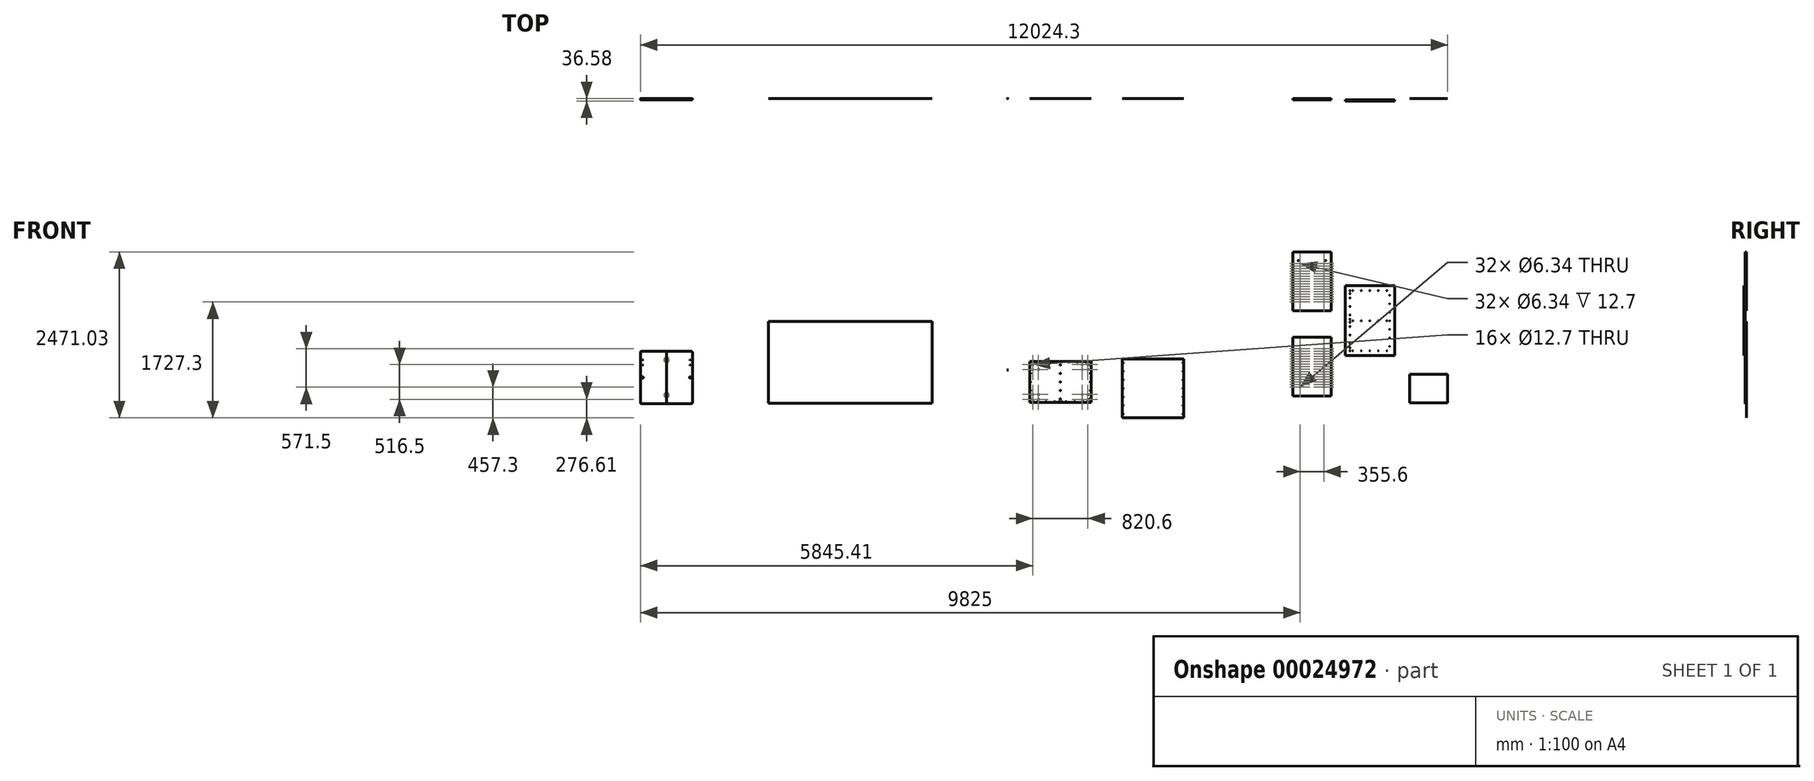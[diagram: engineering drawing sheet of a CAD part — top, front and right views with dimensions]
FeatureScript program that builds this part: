
annotation { "Feature Type Name" : "Feature", "Feature Type Description" : "" }
export const myFeature = defineFeature(function(context is Context, id is Id, definition is map)
    precondition{}
    {
        {
            var Q0;
            Q0=qCreatedBy(makeId("Front.planeOp"),FACE);
            var sketch = newSketch(context, id + "F0", { "sketchPlane" : qUnion([Q0])});
            skLineSegment(sketch, "E0.bottom", {"start": v(-504.26, 364.41) * mm, "end": v(54.54, 364.41) * mm});
            skLineSegment(sketch, "E0.top", {"start": v(-504.26, -245.19) * mm, "end": v(54.54, -245.19) * mm});
            skLineSegment(sketch, "E0.left", {"start": v(-529.66, 339.01) * mm, "end": v(-529.66, -219.79) * mm});
            skLineSegment(sketch, "E0.right", {"start": v(79.94, 339.01) * mm, "end": v(79.94, -219.79) * mm});
            skPoint(sketch, "E1.visualSharp", {"position": v(-529.66, 364.41) * mm});
            skArc(sketch, "E1.filletArc", {"start": v(-504.26, 364.41) * mm, "mid": v(-522.22, 356.97) * mm, "end": v(-529.66, 339.01) * mm});
            skPoint(sketch, "E2.visualSharp", {"position": v(79.94, 364.41) * mm});
            skArc(sketch, "E2.filletArc", {"start": v(79.94, 339.01) * mm, "mid": v(72.5, 356.97) * mm, "end": v(54.54, 364.41) * mm});
            skPoint(sketch, "E3.visualSharp", {"position": v(-529.66, -245.19) * mm});
            skArc(sketch, "E3.filletArc", {"start": v(-529.66, -219.79) * mm, "mid": v(-522.22, -237.75) * mm, "end": v(-504.26, -245.19) * mm});
            skPoint(sketch, "E4.visualSharp", {"position": v(79.94, -245.19) * mm});
            skArc(sketch, "E4.filletArc", {"start": v(54.54, -245.19) * mm, "mid": v(72.5, -237.75) * mm, "end": v(79.94, -219.79) * mm});
            skLineSegment(sketch, "E5.bottom", {"start": v(-529.66, 364.41) * mm, "end": v(-491.56, 364.41) * mm});
            skLineSegment(sketch, "E5.top", {"start": v(-529.66, 361.24) * mm, "end": v(-491.56, 361.24) * mm});
            skLineSegment(sketch, "E5.left", {"start": v(-529.66, 364.41) * mm, "end": v(-529.66, 361.24) * mm});
            skLineSegment(sketch, "E5.right", {"start": v(-491.56, 364.41) * mm, "end": v(-491.56, 361.24) * mm});
            skLineSegment(sketch, "E6.bottom", {"start": v(79.94, 364.41) * mm, "end": v(41.84, 364.41) * mm});
            skLineSegment(sketch, "E6.top", {"start": v(79.94, 361.24) * mm, "end": v(41.84, 361.24) * mm});
            skLineSegment(sketch, "E6.left", {"start": v(79.94, 364.41) * mm, "end": v(79.94, 361.24) * mm});
            skLineSegment(sketch, "E6.right", {"start": v(41.84, 364.41) * mm, "end": v(41.84, 361.24) * mm});
            skSolve(sketch);
        }
        {
            var Q0;
            {var subQ0=sQuery(id+"F0.wireOp",EDGE,"E5.left");Q0=makeQuery(id+"F0.imprint","IMPRINT",FACE,{"disambiguationData":[TD([[makeQuery(id+"F0.imprint","IMPRINT",EDGE,{"derivedFrom":subQ0}),1.0]])]});}
            var Q1;
            Q1=makeQuery(id+"F0.imprint","IMPRINT",FACE,{"disambiguationData":[TD([[makeQuery(id+"F0.imprint","IMPRINT",EDGE,{"derivedFrom":sQuery(id+"F0.wireOp",EDGE,"E0.bottom")}),-1.0]])]});
            var Q2;
            {var subQ0=sQuery(id+"F0.wireOp",EDGE,"E5.right");Q2=makeQuery(id+"F0.imprint","IMPRINT",FACE,{"disambiguationData":[TD([[makeQuery(id+"F0.imprint","IMPRINT",EDGE,{"derivedFrom":subQ0}),-1.0]])]});}
            extrude(context, id + "F1", {"entities" : qUnion([Q0, Q1, Q2]), "depth" : 23 / 812.8 * mm});
        }
        {
            var Q0;
            Q0=qCreatedBy(makeId("Front.planeOp"),FACE);
            var sketch = newSketch(context, id + "F2", { "sketchPlane" : qUnion([Q0])});
            skLineSegment(sketch, "E7.bottom", {"start": v(382.88, 489.15) * mm, "end": v(1297.28, 489.15) * mm});
            skLineSegment(sketch, "E7.top", {"start": v(382.88, -120.45) * mm, "end": v(1297.28, -120.45) * mm});
            skLineSegment(sketch, "E7.left", {"start": v(382.88, 489.15) * mm, "end": v(382.88, -120.45) * mm});
            skLineSegment(sketch, "E7.right", {"start": v(1297.28, 489.15) * mm, "end": v(1297.28, -120.45) * mm});
            skSolve(sketch);
        }
        {
            var Q0;
            Q0 = qSketchRegion(id + "F2", true);
            extrude(context, id + "F3", {"entities" : qUnion([Q0]), "depth" : 23 / 812.8 * mm});
        }
        {
            var Q0;
            Q0=qCreatedBy(makeId("Front.planeOp"),FACE);
            var sketch = newSketch(context, id + "F4", { "sketchPlane" : qUnion([Q0])});
            skLineSegment(sketch, "E8.bottom", {"start": v(1763.98, 527.36) * mm, "end": v(2678.38, 527.36) * mm});
            skLineSegment(sketch, "E8.top", {"start": v(1763.98, -350.51) * mm, "end": v(2678.38, -350.51) * mm});
            skLineSegment(sketch, "E8.left", {"start": v(1763.98, 527.36) * mm, "end": v(1763.98, -350.51) * mm});
            skLineSegment(sketch, "E8.right", {"start": v(2678.38, 527.36) * mm, "end": v(2678.38, -350.51) * mm});
            skSolve(sketch);
        }
        {
            var Q0;
            Q0=makeQuery(id+"F4.imprint","IMPRINT",FACE,{"disambiguationData":[TD([[makeQuery(id+"F4.imprint","IMPRINT",EDGE,{"derivedFrom":sQuery(id+"F4.wireOp",EDGE,"E8.bottom")}),-1.0]])]});
            extrude(context, id + "F5", {"entities" : qUnion([Q0]), "depth" : 23 / 812.8 * mm});
        }
        {
            var Q0;
            Q0=qCreatedBy(makeId("Front.planeOp"),FACE);
            var sketch = newSketch(context, id + "F6", { "sketchPlane" : qUnion([Q0])});
            skLineSegment(sketch, "E9.bottom", {"start": v(4301.03, 850.52) * mm, "end": v(4873.31, 850.52) * mm});
            skLineSegment(sketch, "E9.top", {"start": v(4301.03, -27.35) * mm, "end": v(4873.31, -27.35) * mm});
            skLineSegment(sketch, "E9.left", {"start": v(4301.03, 850.52) * mm, "end": v(4301.03, -27.35) * mm});
            skLineSegment(sketch, "E9.right", {"start": v(4873.31, 850.52) * mm, "end": v(4873.31, -27.35) * mm});
            skCircle(sketch, "E10", {"center": v(4383.97, 723.52) * mm, "radius": 3.97 * mm});
            skCircle(sketch, "E11", {"center": v(4790.37, 723.52) * mm, "radius": 3.97 * mm});
            skPoint(sketch, "E12", {"position": v(4587.17, 850.52) * mm});
            skCircle(sketch, "E13", {"center": v(4409.37, 106.79) * mm, "radius": 3.17 * mm});
            skCircle(sketch, "E14.0.1.0", {"center": v(4409.37, 144.89) * mm, "radius": 3.17 * mm});
            skCircle(sketch, "E14.0.2.0", {"center": v(4409.37, 182.99) * mm, "radius": 3.17 * mm});
            skCircle(sketch, "E14.0.3.0", {"center": v(4409.37, 221.09) * mm, "radius": 3.17 * mm});
            skCircle(sketch, "E14.0.4.0", {"center": v(4409.37, 259.19) * mm, "radius": 3.17 * mm});
            skCircle(sketch, "E14.0.5.0", {"center": v(4409.37, 297.29) * mm, "radius": 3.17 * mm});
            skCircle(sketch, "E14.0.6.0", {"center": v(4409.37, 335.39) * mm, "radius": 3.17 * mm});
            skCircle(sketch, "E14.0.7.0", {"center": v(4409.37, 373.49) * mm, "radius": 3.17 * mm});
            skCircle(sketch, "E14.0.8.0", {"center": v(4409.37, 411.59) * mm, "radius": 3.17 * mm});
            skCircle(sketch, "E14.0.9.0", {"center": v(4409.37, 449.69) * mm, "radius": 3.17 * mm});
            skCircle(sketch, "E14.0.10.0", {"center": v(4409.37, 487.79) * mm, "radius": 3.17 * mm});
            skCircle(sketch, "E14.0.11.0", {"center": v(4409.37, 525.89) * mm, "radius": 3.17 * mm});
            skCircle(sketch, "E14.0.12.0", {"center": v(4409.37, 563.99) * mm, "radius": 3.17 * mm});
            skCircle(sketch, "E14.0.13.0", {"center": v(4409.37, 602.09) * mm, "radius": 3.17 * mm});
            skCircle(sketch, "E14.0.14.0", {"center": v(4409.37, 640.19) * mm, "radius": 3.17 * mm});
            skCircle(sketch, "E14.0.15.0", {"center": v(4409.37, 678.29) * mm, "radius": 3.17 * mm});
            skCircle(sketch, "E14.1.0.0", {"center": v(4764.97, 106.79) * mm, "radius": 3.17 * mm});
            skCircle(sketch, "E14.1.1.0", {"center": v(4764.97, 144.89) * mm, "radius": 3.17 * mm});
            skCircle(sketch, "E14.1.2.0", {"center": v(4764.97, 182.99) * mm, "radius": 3.17 * mm});
            skCircle(sketch, "E14.1.3.0", {"center": v(4764.97, 221.09) * mm, "radius": 3.17 * mm});
            skCircle(sketch, "E14.1.4.0", {"center": v(4764.97, 259.19) * mm, "radius": 3.17 * mm});
            skCircle(sketch, "E14.1.5.0", {"center": v(4764.97, 297.29) * mm, "radius": 3.17 * mm});
            skCircle(sketch, "E14.1.6.0", {"center": v(4764.97, 335.39) * mm, "radius": 3.17 * mm});
            skCircle(sketch, "E14.1.7.0", {"center": v(4764.97, 373.49) * mm, "radius": 3.17 * mm});
            skCircle(sketch, "E14.1.8.0", {"center": v(4764.97, 411.59) * mm, "radius": 3.17 * mm});
            skCircle(sketch, "E14.1.9.0", {"center": v(4764.97, 449.69) * mm, "radius": 3.17 * mm});
            skCircle(sketch, "E14.1.10.0", {"center": v(4764.97, 487.79) * mm, "radius": 3.17 * mm});
            skCircle(sketch, "E14.1.11.0", {"center": v(4764.97, 525.89) * mm, "radius": 3.17 * mm});
            skCircle(sketch, "E14.1.12.0", {"center": v(4764.97, 563.99) * mm, "radius": 3.17 * mm});
            skCircle(sketch, "E14.1.13.0", {"center": v(4764.97, 602.09) * mm, "radius": 3.17 * mm});
            skCircle(sketch, "E14.1.14.0", {"center": v(4764.97, 640.19) * mm, "radius": 3.17 * mm});
            skCircle(sketch, "E14.1.15.0", {"center": v(4764.97, 678.29) * mm, "radius": 3.17 * mm});
            skLineSegment(sketch, "E14.direction1", {"start": v(4409.37, 106.79) * mm, "end": v(4764.97, 106.79) * mm, "construction": true});
            skLineSegment(sketch, "E14.direction2", {"start": v(4409.37, 106.79) * mm, "end": v(4409.37, 144.89) * mm, "construction": true});
            skSolve(sketch);
        }
        {
            var Q0;
            Q0=makeQuery(id+"F6.imprint","IMPRINT",FACE,{"disambiguationData":[TD([[makeQuery(id+"F6.imprint","IMPRINT",EDGE,{"derivedFrom":sQuery(id+"F6.wireOp",EDGE,"E9.bottom")}),-1.0]])]});
            extrude(context, id + "F7", {"entities" : qUnion([Q0]), "depth" : 23 / 812.8 * mm});
        }
        {
            var Q0;
            Q0=makeQuery(id+"F7.opExtrude","SWEPT_BODY",BODY,{"disambiguationData":[OSD([sQuery(id+"F6.wireOp",EDGE,"E9.bottom"),sQuery(id+"F6.wireOp",EDGE,"E9.top"),sQuery(id+"F6.wireOp",EDGE,"E9.left"),sQuery(id+"F6.wireOp",EDGE,"E9.right")])]});
            transform(context, id + "F8", {"entities" : qUnion([Q0]), "transformType" : TransformType.TRANSLATION_3D, "dx" : 914.4 * mm, "dy" : 0 * mm, "dz" : 0 * mm, "makeCopy" : true});
        }
        {
            var Q0;
            Q0=makeQuery(id+"F8.opPattern","COPY",BODY,{"derivedFrom":makeQuery(id+"F7.opExtrude","SWEPT_BODY",BODY,{"disambiguationData":[OSD([sQuery(id+"F6.wireOp",EDGE,"E9.bottom"),sQuery(id+"F6.wireOp",EDGE,"E9.top"),sQuery(id+"F6.wireOp",EDGE,"E9.left"),sQuery(id+"F6.wireOp",EDGE,"E9.right")])]}),"instanceName":"1"});
            transform(context, id + "F9", {"entities" : qUnion([Q0]), "transformType" : TransformType.TRANSLATION_3D, "dx" : 0 * mm, "dy" : 0 * mm, "dz" : 0 * mm, "makeCopy" : true});
        }
        {
            var Q0;
            Q0=makeQuery(id+"F9.opPattern","COPY",BODY,{"derivedFrom":makeQuery(id+"F8.opPattern","COPY",BODY,{"derivedFrom":makeQuery(id+"F7.opExtrude","SWEPT_BODY",BODY,{"disambiguationData":[OSD([sQuery(id+"F6.wireOp",EDGE,"E9.bottom"),sQuery(id+"F6.wireOp",EDGE,"E9.top"),sQuery(id+"F6.wireOp",EDGE,"E9.left"),sQuery(id+"F6.wireOp",EDGE,"E9.right")])]}),"instanceName":"1"}),"instanceName":"1"});
            deleteBodies(context, id + "F10", {"entities" : qUnion([Q0])});
        }
        {
            var Q0;
            Q0=makeQuery(id+"F8.opPattern","COPY",BODY,{"derivedFrom":makeQuery(id+"F7.opExtrude","SWEPT_BODY",BODY,{"disambiguationData":[OSD([sQuery(id+"F6.wireOp",EDGE,"E9.bottom"),sQuery(id+"F6.wireOp",EDGE,"E9.top"),sQuery(id+"F6.wireOp",EDGE,"E9.left"),sQuery(id+"F6.wireOp",EDGE,"E9.right")])]}),"instanceName":"1"});
            transform(context, id + "F11", {"entities" : qUnion([Q0]), "transformType" : TransformType.TRANSLATION_3D, "dx" : 914.4 * mm, "dy" : 0 * mm, "dz" : 0 * mm, "makeCopy" : true});
        }
        {
            var Q0;
            Q0=makeQuery(id+"F11.opPattern","COPY",FACE,{"derivedFrom":makeQuery(id+"F8.opPattern","COPY",FACE,{"derivedFrom":makeQuery(id+"F7.opExtrude","CAP_FACE",FACE,{"disambiguationData":[OSD([sQuery(id+"F6.wireOp",EDGE,"E9.bottom"),sQuery(id+"F6.wireOp",EDGE,"E9.top"),sQuery(id+"F6.wireOp",EDGE,"E9.left"),sQuery(id+"F6.wireOp",EDGE,"E9.right")])],"isStart":false}),"instanceName":"1"}),"instanceName":"1"});
            var sketch = newSketch(context, id + "F12", { "sketchPlane" : qUnion([Q0])});
            skLineSegment(sketch, "E15.bottom", {"start": v(6040.38, 295.61) * mm, "end": v(6608.7, 295.61) * mm});
            skLineSegment(sketch, "E15.top", {"start": v(6040.38, -129.84) * mm, "end": v(6608.7, -129.84) * mm});
            skLineSegment(sketch, "E15.left", {"start": v(6040.38, 295.61) * mm, "end": v(6040.38, -129.84) * mm});
            skLineSegment(sketch, "E15.right", {"start": v(6608.7, 295.61) * mm, "end": v(6608.7, -129.84) * mm});
            skSolve(sketch);
        }
        {
            var Q0;
            Q0 = qSketchRegion(id + "F12", true);
            extrude(context, id + "F13", {"entities" : qUnion([Q0]), "depth" : 23 / 812.8 * mm});
        }
        {
            var Q0;
            {var subQ0=sQuery(id+"F0.wireOp",EDGE,"E5.right");Q0=makeQuery(id+"F0.imprint","IMPRINT",FACE,{"disambiguationData":[TD([[makeQuery(id+"F0.imprint","IMPRINT",EDGE,{"derivedFrom":subQ0}),-1.0]])]});}
            extrude(context, id + "F14", {"entities" : qUnion([Q0]), "operationType" : NewBodyOperationType.REMOVE, "oppositeDirection" : true, "depth" : 25.4 * mm});
        }
        {
            var Q0;
            {var subQ0=sQuery(id+"F0.wireOp",EDGE,"E5.left");Q0=makeQuery(id+"F0.imprint","IMPRINT",FACE,{"disambiguationData":[TD([[makeQuery(id+"F0.imprint","IMPRINT",EDGE,{"derivedFrom":subQ0}),1.0]])]});}
            var Q1;
            {var subQ0=sQuery(id+"F0.wireOp",EDGE,"E5.right");Q1=makeQuery(id+"F0.imprint","IMPRINT",FACE,{"disambiguationData":[TD([[makeQuery(id+"F0.imprint","IMPRINT",EDGE,{"derivedFrom":subQ0}),-1.0]])]});}
            extrude(context, id + "F15", {"entities" : qUnion([Q0, Q1]), "depth" : 23 / 812.8 * mm});
        }
        {
            var Q0;
            Q0=makeQuery(id+"F15.opExtrude","SWEPT_BODY",BODY,{"disambiguationData":[OSD([sQuery(id+"F0.wireOp",EDGE,"E5.bottom"),sQuery(id+"F0.wireOp",EDGE,"E5.top"),sQuery(id+"F0.wireOp",EDGE,"E5.left"),sQuery(id+"F0.wireOp",EDGE,"E5.right")])]});
            var Q1;
            Q1=makeQuery(id+"F1.opExtrude","SWEPT_BODY",BODY,{"disambiguationData":[OSD([sQuery(id+"F0.wireOp",EDGE,"E0.bottom"),sQuery(id+"F0.wireOp",EDGE,"E0.top"),sQuery(id+"F0.wireOp",EDGE,"E0.left"),sQuery(id+"F0.wireOp",EDGE,"E0.right"),sQuery(id+"F0.wireOp",EDGE,"E1.filletArc"),sQuery(id+"F0.wireOp",EDGE,"E2.filletArc"),sQuery(id+"F0.wireOp",EDGE,"E3.filletArc"),sQuery(id+"F0.wireOp",EDGE,"E4.filletArc"),sQuery(id+"F0.wireOp",EDGE,"E5.bottom"),sQuery(id+"F0.wireOp",EDGE,"E5.top"),sQuery(id+"F0.wireOp",EDGE,"E5.left")])]});
            booleanBodies(context, id + "F16", {"operationType" : BooleanOperationType.SUBTRACTION, "tools" : qUnion([Q0]), "targets" : qUnion([Q1])});
        }
        {
            var Q0;
            Q0=makeQuery(id+"F5.opExtrude","SWEPT_BODY",BODY,{"disambiguationData":[OSD([sQuery(id+"F4.wireOp",EDGE,"E8.bottom"),sQuery(id+"F4.wireOp",EDGE,"E8.top"),sQuery(id+"F4.wireOp",EDGE,"E8.left"),sQuery(id+"F4.wireOp",EDGE,"E8.right")])]});
            transform(context, id + "F17", {"entities" : qUnion([Q0]), "transformType" : TransformType.TRANSLATION_3D, "dx" : 5080 * mm, "dy" : 0 * mm, "dz" : 0 * mm, "makeCopy" : true});
        }
        {
            var Q0;
            Q0=makeQuery(id+"F17.opPattern","COPY",BODY,{"derivedFrom":makeQuery(id+"F5.opExtrude","SWEPT_BODY",BODY,{"disambiguationData":[OSD([sQuery(id+"F4.wireOp",EDGE,"E8.bottom"),sQuery(id+"F4.wireOp",EDGE,"E8.top"),sQuery(id+"F4.wireOp",EDGE,"E8.left"),sQuery(id+"F4.wireOp",EDGE,"E8.right")])]}),"instanceName":"1"});
            deleteBodies(context, id + "F18", {"entities" : qUnion([Q0])});
        }
        {
            var Q0;
            Q0=makeQuery(id+"F13.opExtrude","CAP_FACE",FACE,{"disambiguationData":[OSD([sQuery(id+"F12.wireOp",EDGE,"E15.bottom"),sQuery(id+"F12.wireOp",EDGE,"E15.top"),sQuery(id+"F12.wireOp",EDGE,"E15.left"),sQuery(id+"F12.wireOp",EDGE,"E15.right")])],"isStart":false});
            var sketch = newSketch(context, id + "F19", { "sketchPlane" : qUnion([Q0])});
            skLineSegment(sketch, "E16.bottom", {"start": v(6912.5, 591.54) * mm, "end": v(7826.9, 591.54) * mm});
            skLineSegment(sketch, "E16.top", {"start": v(6912.5, -304.59) * mm, "end": v(7826.9, -304.59) * mm});
            skLineSegment(sketch, "E16.left", {"start": v(6912.5, 591.54) * mm, "end": v(6912.5, -304.59) * mm});
            skLineSegment(sketch, "E16.right", {"start": v(7826.9, 591.54) * mm, "end": v(7826.9, -304.59) * mm});
            skSolve(sketch);
        }
        {
            var Q0;
            Q0 = qSketchRegion(id + "F19", true);
            extrude(context, id + "F20", {"entities" : qUnion([Q0]), "depth" : 18.26 * mm});
        }
        {
            var Q0;
            Q0=makeQuery(id+"F20.opExtrude","CAP_FACE",FACE,{"disambiguationData":[OSD([sQuery(id+"F19.wireOp",EDGE,"E16.bottom"),sQuery(id+"F19.wireOp",EDGE,"E16.top"),sQuery(id+"F19.wireOp",EDGE,"E16.left"),sQuery(id+"F19.wireOp",EDGE,"E16.right")])],"isStart":false});
            var sketch = newSketch(context, id + "F21", { "sketchPlane" : qUnion([Q0])});
            skLineSegment(sketch, "E17.bottom", {"start": v(5080.39, 1616.94) * mm, "end": v(5816.99, 1616.94) * mm});
            skLineSegment(sketch, "E17.top", {"start": v(5080.39, 575.54) * mm, "end": v(5816.99, 575.54) * mm});
            skLineSegment(sketch, "E17.left", {"start": v(5080.39, 1616.94) * mm, "end": v(5080.39, 575.54) * mm});
            skLineSegment(sketch, "E17.right", {"start": v(5816.99, 1616.94) * mm, "end": v(5816.99, 575.54) * mm});
            skSolve(sketch);
        }
        {
            var Q0;
            Q0 = qSketchRegion(id + "F21", true);
            extrude(context, id + "F22", {"entities" : qUnion([Q0]), "depth" : 18.26 * mm});
        }
        {
            var Q0;
            Q0=makeQuery(id+"F1.opExtrude","CAP_FACE",FACE,{"disambiguationData":[OSD([sQuery(id+"F0.wireOp",EDGE,"E0.bottom"),sQuery(id+"F0.wireOp",EDGE,"E0.top"),sQuery(id+"F0.wireOp",EDGE,"E0.left"),sQuery(id+"F0.wireOp",EDGE,"E0.right"),sQuery(id+"F0.wireOp",EDGE,"E1.filletArc"),sQuery(id+"F0.wireOp",EDGE,"E2.filletArc"),sQuery(id+"F0.wireOp",EDGE,"E3.filletArc"),sQuery(id+"F0.wireOp",EDGE,"E4.filletArc"),sQuery(id+"F0.wireOp",EDGE,"E5.bottom"),sQuery(id+"F0.wireOp",EDGE,"E5.top"),sQuery(id+"F0.wireOp",EDGE,"E5.left"),sQuery(id+"F0.wireOp",EDGE,"E6.top"),sQuery(id+"F0.wireOp",EDGE,"E6.right")])],"isStart":true});
            fillet(context, id + "F23", {"entities" : qUnion([Q0]), "radius" : 12.7 * mm, "tangentPropagation" : true, "allowEdgeOverflow" : false});
        }
        {
            var Q0;
            Q0=makeQuery(id+"F7.opExtrude","SWEPT_BODY",BODY,{"disambiguationData":[OSD([sQuery(id+"F6.wireOp",EDGE,"E9.bottom"),sQuery(id+"F6.wireOp",EDGE,"E9.top"),sQuery(id+"F6.wireOp",EDGE,"E9.left"),sQuery(id+"F6.wireOp",EDGE,"E9.right")])]});
            deleteBodies(context, id + "F24", {"entities" : qUnion([Q0])});
        }
        {
            var Q0;
            Q0=makeQuery(id+"F20.opExtrude","SWEPT_BODY",BODY,{"disambiguationData":[OSD([sQuery(id+"F19.wireOp",EDGE,"E16.bottom"),sQuery(id+"F19.wireOp",EDGE,"E16.top"),sQuery(id+"F19.wireOp",EDGE,"E16.left"),sQuery(id+"F19.wireOp",EDGE,"E16.right")])]});
            deleteBodies(context, id + "F25", {"entities" : qUnion([Q0])});
        }
        {
            var Q0;
            Q0=qCreatedBy(makeId("Front.planeOp"),FACE);
            var sketch = newSketch(context, id + "F26", { "sketchPlane" : qUnion([Q0])});
            skLineSegment(sketch, "E18.bottom", {"start": v(-5028.28, 638.26) * mm, "end": v(-4653.63, 638.26) * mm});
            skLineSegment(sketch, "E18.top", {"start": v(-5028.28, -138.02) * mm, "end": v(-4653.63, -138.02) * mm});
            skLineSegment(sketch, "E18.left", {"start": v(-5028.28, 638.26) * mm, "end": v(-5028.28, -138.02) * mm});
            skLineSegment(sketch, "E18.right", {"start": v(-4640.93, 625.56) * mm, "end": v(-4640.93, -125.32) * mm});
            skPoint(sketch, "E19.visualSharp", {"position": v(-4640.93, -138.02) * mm});
            skArc(sketch, "E19.filletArc", {"start": v(-4653.63, -138.02) * mm, "mid": v(-4644.65, -134.3) * mm, "end": v(-4640.93, -125.32) * mm});
            skPoint(sketch, "E20.visualSharp", {"position": v(-4640.93, 638.26) * mm});
            skArc(sketch, "E20.filletArc", {"start": v(-4640.93, 625.56) * mm, "mid": v(-4644.65, 634.54) * mm, "end": v(-4653.63, 638.26) * mm});
            skCircle(sketch, "E21", {"center": v(-5007.64, 511.26) * mm, "radius": 17.5 * mm});
            skCircle(sketch, "E22", {"center": v(-5007.64, -11.02) * mm, "radius": 17.5 * mm});
            skCircle(sketch, "E23", {"center": v(-4999.64, 11.48) * mm, "radius": 4 * mm});
            skCircle(sketch, "E24", {"center": v(-4999.64, -33.52) * mm, "radius": 4 * mm});
            skCircle(sketch, "E25", {"center": v(-4999.64, 488.75) * mm, "radius": 4 * mm});
            skCircle(sketch, "E26", {"center": v(-4999.64, 533.76) * mm, "radius": 4 * mm});
            skCircle(sketch, "E27", {"center": v(-4675.85, 250.12) * mm, "radius": 9.52 * mm});
            skPoint(sketch, "E28", {"position": v(-4640.93, 250.12) * mm});
            skCircle(sketch, "E29", {"center": v(-4675.85, 435.06) * mm, "radius": 2.38 * mm});
            skCircle(sketch, "E30", {"center": v(-4675.85, 511.26) * mm, "radius": 2.38 * mm});
            skSolve(sketch);
        }
        {
            var Q0;
            Q0 = qSketchRegion(id + "F26", true);
            var Q1;
            Q1=makeQuery(id+"F26.imprint","IMPRINT",FACE,{"disambiguationData":[TD([[makeQuery(id+"F26.imprint","IMPRINT",EDGE,{"derivedFrom":sQuery(id+"F26.wireOp",EDGE,"E22")}),1.0]])]});
            var Q2;
            Q2=makeQuery(id+"F26.imprint","IMPRINT",FACE,{"disambiguationData":[TD([[makeQuery(id+"F26.imprint","IMPRINT",EDGE,{"derivedFrom":sQuery(id+"F26.wireOp",EDGE,"E23")}),1.0]])]});
            var Q3;
            Q3=makeQuery(id+"F26.imprint","IMPRINT",FACE,{"disambiguationData":[TD([[makeQuery(id+"F26.imprint","IMPRINT",EDGE,{"derivedFrom":sQuery(id+"F26.wireOp",EDGE,"E24")}),1.0]])]});
            var Q4;
            Q4=makeQuery(id+"F26.imprint","IMPRINT",FACE,{"disambiguationData":[TD([[makeQuery(id+"F26.imprint","IMPRINT",EDGE,{"derivedFrom":sQuery(id+"F26.wireOp",EDGE,"E21")}),1.0]])]});
            var Q5;
            Q5=makeQuery(id+"F26.imprint","IMPRINT",FACE,{"disambiguationData":[TD([[makeQuery(id+"F26.imprint","IMPRINT",EDGE,{"derivedFrom":sQuery(id+"F26.wireOp",EDGE,"E26")}),1.0]])]});
            var Q6;
            Q6=makeQuery(id+"F26.imprint","IMPRINT",FACE,{"disambiguationData":[TD([[makeQuery(id+"F26.imprint","IMPRINT",EDGE,{"derivedFrom":sQuery(id+"F26.wireOp",EDGE,"E25")}),1.0]])]});
            extrude(context, id + "F27", {"entities" : qUnion([Q0, Q1, Q2, Q3, Q4, Q5, Q6]), "depth" : 18.26 * mm});
        }
        {
            var Q0;
            Q0=makeQuery(id+"F27.opExtrude","CAP_EDGE",EDGE,{"disambiguationData":[OSD([sQuery(id+"F26.wireOp",EDGE,"E18.top")])],"isStart":true});
            var Q1;
            Q1=makeQuery(id+"F27.opExtrude","CAP_EDGE",EDGE,{"disambiguationData":[OSD([sQuery(id+"F26.wireOp",EDGE,"E18.right")])],"isStart":true});
            var Q2;
            Q2=makeQuery(id+"F27.opExtrude","CAP_EDGE",EDGE,{"disambiguationData":[OSD([sQuery(id+"F26.wireOp",EDGE,"E18.bottom")])],"isStart":true});
            fillet(context, id + "F28", {"entities" : qUnion([Q0, Q1, Q2]), "radius" : 6.35 * mm, "tangentPropagation" : true, "allowEdgeOverflow" : false});
        }
        {
            var Q0;
            Q0=makeQuery(id+"F27.opExtrude","CAP_EDGE",EDGE,{"disambiguationData":[OSD([sQuery(id+"F26.wireOp",EDGE,"E18.top")])],"isStart":false});
            var Q1;
            Q1=makeQuery(id+"F27.opExtrude","CAP_EDGE",EDGE,{"disambiguationData":[OSD([sQuery(id+"F26.wireOp",EDGE,"E18.right")])],"isStart":false});
            var Q2;
            Q2=makeQuery(id+"F27.opExtrude","CAP_EDGE",EDGE,{"disambiguationData":[OSD([sQuery(id+"F26.wireOp",EDGE,"E18.bottom")])],"isStart":false});
            fillet(context, id + "F29", {"entities" : qUnion([Q0, Q1, Q2]), "radius" : 6.35 * mm, "tangentPropagation" : true, "allowEdgeOverflow" : false});
        }
        {
            var Q0;
            Q0=makeQuery(id+"F26.imprint","IMPRINT",FACE,{"disambiguationData":[TD([[makeQuery(id+"F26.imprint","IMPRINT",EDGE,{"derivedFrom":sQuery(id+"F26.wireOp",EDGE,"E21")}),1.0]])]});
            extrude(context, id + "F30", {"entities" : qUnion([Q0]), "operationType" : NewBodyOperationType.REMOVE, "depth" : 12.7 * mm});
        }
        {
            var Q0;
            Q0=makeQuery(id+"F26.imprint","IMPRINT",FACE,{"disambiguationData":[TD([[makeQuery(id+"F26.imprint","IMPRINT",EDGE,{"derivedFrom":sQuery(id+"F26.wireOp",EDGE,"E25")}),1.0]])]});
            var Q1;
            Q1=makeQuery(id+"F26.imprint","IMPRINT",FACE,{"disambiguationData":[TD([[makeQuery(id+"F26.imprint","IMPRINT",EDGE,{"derivedFrom":sQuery(id+"F26.wireOp",EDGE,"E26")}),1.0]])]});
            extrude(context, id + "F31", {"entities" : qUnion([Q0, Q1]), "operationType" : NewBodyOperationType.REMOVE, "depth" : 12.7 * mm});
        }
        {
            var Q0;
            Q0=makeQuery(id+"F26.imprint","IMPRINT",FACE,{"disambiguationData":[TD([[makeQuery(id+"F26.imprint","IMPRINT",EDGE,{"derivedFrom":sQuery(id+"F26.wireOp",EDGE,"E22")}),1.0]])]});
            var Q1;
            Q1=makeQuery(id+"F26.imprint","IMPRINT",FACE,{"disambiguationData":[TD([[makeQuery(id+"F26.imprint","IMPRINT",EDGE,{"derivedFrom":sQuery(id+"F26.wireOp",EDGE,"E23")}),1.0]])]});
            var Q2;
            Q2=makeQuery(id+"F26.imprint","IMPRINT",FACE,{"disambiguationData":[TD([[makeQuery(id+"F26.imprint","IMPRINT",EDGE,{"derivedFrom":sQuery(id+"F26.wireOp",EDGE,"E24")}),1.0]])]});
            extrude(context, id + "F32", {"entities" : qUnion([Q0, Q1, Q2]), "operationType" : NewBodyOperationType.REMOVE, "depth" : 12.7 * mm});
        }
        {
            var Q0;
            Q0=makeQuery(id+"F11.opPattern","COPY",BODY,{"derivedFrom":makeQuery(id+"F8.opPattern","COPY",BODY,{"derivedFrom":makeQuery(id+"F7.opExtrude","SWEPT_BODY",BODY,{"disambiguationData":[OSD([sQuery(id+"F6.wireOp",EDGE,"E9.bottom"),sQuery(id+"F6.wireOp",EDGE,"E9.top"),sQuery(id+"F6.wireOp",EDGE,"E9.left"),sQuery(id+"F6.wireOp",EDGE,"E9.right"),sQuery(id+"F6.wireOp",EDGE,"E10"),sQuery(id+"F6.wireOp",EDGE,"E11")])]}),"instanceName":"1"}),"instanceName":"1"});
            deleteBodies(context, id + "F33", {"entities" : qUnion([Q0])});
        }
        {
            var Q0;
            Q0=makeQuery(id+"F6.imprint","IMPRINT",FACE,{"disambiguationData":[TD([[makeQuery(id+"F6.imprint","IMPRINT",EDGE,{"derivedFrom":sQuery(id+"F6.wireOp",EDGE,"E14.1.8.0")}),1.0]])]});
            var Q1;
            Q1=makeQuery(id+"F6.imprint","IMPRINT",FACE,{"disambiguationData":[TD([[makeQuery(id+"F6.imprint","IMPRINT",EDGE,{"derivedFrom":sQuery(id+"F6.wireOp",EDGE,"E14.1.7.0")}),1.0]])]});
            var Q2;
            Q2=makeQuery(id+"F6.imprint","IMPRINT",FACE,{"disambiguationData":[TD([[makeQuery(id+"F6.imprint","IMPRINT",EDGE,{"derivedFrom":sQuery(id+"F6.wireOp",EDGE,"E14.1.6.0")}),1.0]])]});
            var Q3;
            Q3=makeQuery(id+"F6.imprint","IMPRINT",FACE,{"disambiguationData":[TD([[makeQuery(id+"F6.imprint","IMPRINT",EDGE,{"derivedFrom":sQuery(id+"F6.wireOp",EDGE,"E14.1.4.0")}),1.0]])]});
            var Q4;
            Q4=makeQuery(id+"F6.imprint","IMPRINT",FACE,{"disambiguationData":[TD([[makeQuery(id+"F6.imprint","IMPRINT",EDGE,{"derivedFrom":sQuery(id+"F6.wireOp",EDGE,"E14.1.10.0")}),1.0]])]});
            var Q5;
            Q5=makeQuery(id+"F6.imprint","IMPRINT",FACE,{"disambiguationData":[TD([[makeQuery(id+"F6.imprint","IMPRINT",EDGE,{"derivedFrom":sQuery(id+"F6.wireOp",EDGE,"E14.1.2.0")}),1.0]])]});
            var Q6;
            Q6=makeQuery(id+"F6.imprint","IMPRINT",FACE,{"disambiguationData":[TD([[makeQuery(id+"F6.imprint","IMPRINT",EDGE,{"derivedFrom":sQuery(id+"F6.wireOp",EDGE,"E14.1.1.0")}),1.0]])]});
            var Q7;
            Q7=makeQuery(id+"F6.imprint","IMPRINT",FACE,{"disambiguationData":[TD([[makeQuery(id+"F6.imprint","IMPRINT",EDGE,{"derivedFrom":sQuery(id+"F6.wireOp",EDGE,"E14.1.14.0")}),1.0]])]});
            var Q8;
            Q8=makeQuery(id+"F6.imprint","IMPRINT",FACE,{"disambiguationData":[TD([[makeQuery(id+"F6.imprint","IMPRINT",EDGE,{"derivedFrom":sQuery(id+"F6.wireOp",EDGE,"E14.1.3.0")}),1.0]])]});
            var Q9;
            Q9=makeQuery(id+"F6.imprint","IMPRINT",FACE,{"disambiguationData":[TD([[makeQuery(id+"F6.imprint","IMPRINT",EDGE,{"derivedFrom":sQuery(id+"F6.wireOp",EDGE,"E14.1.11.0")}),1.0]])]});
            var Q10;
            Q10=makeQuery(id+"F6.imprint","IMPRINT",FACE,{"disambiguationData":[TD([[makeQuery(id+"F6.imprint","IMPRINT",EDGE,{"derivedFrom":sQuery(id+"F6.wireOp",EDGE,"E14.1.12.0")}),1.0]])]});
            var Q11;
            Q11=makeQuery(id+"F6.imprint","IMPRINT",FACE,{"disambiguationData":[TD([[makeQuery(id+"F6.imprint","IMPRINT",EDGE,{"derivedFrom":sQuery(id+"F6.wireOp",EDGE,"E14.1.15.0")}),1.0]])]});
            var Q12;
            Q12=makeQuery(id+"F6.imprint","IMPRINT",FACE,{"disambiguationData":[TD([[makeQuery(id+"F6.imprint","IMPRINT",EDGE,{"derivedFrom":sQuery(id+"F6.wireOp",EDGE,"E14.1.9.0")}),1.0]])]});
            var Q13;
            Q13=makeQuery(id+"F6.imprint","IMPRINT",FACE,{"disambiguationData":[TD([[makeQuery(id+"F6.imprint","IMPRINT",EDGE,{"derivedFrom":sQuery(id+"F6.wireOp",EDGE,"E14.1.5.0")}),1.0]])]});
            var Q14;
            Q14=makeQuery(id+"F6.imprint","IMPRINT",FACE,{"disambiguationData":[TD([[makeQuery(id+"F6.imprint","IMPRINT",EDGE,{"derivedFrom":sQuery(id+"F6.wireOp",EDGE,"E14.1.13.0")}),1.0]])]});
            var Q15;
            Q15=makeQuery(id+"F6.imprint","IMPRINT",FACE,{"disambiguationData":[TD([[makeQuery(id+"F6.imprint","IMPRINT",EDGE,{"derivedFrom":sQuery(id+"F6.wireOp",EDGE,"E14.1.0.0")}),1.0]])]});
            var Q16;
            Q16=makeQuery(id+"F6.imprint","IMPRINT",FACE,{"disambiguationData":[TD([[makeQuery(id+"F6.imprint","IMPRINT",EDGE,{"derivedFrom":sQuery(id+"F6.wireOp",EDGE,"E14.0.11.0")}),1.0]])]});
            var Q17;
            Q17=makeQuery(id+"F6.imprint","IMPRINT",FACE,{"disambiguationData":[TD([[makeQuery(id+"F6.imprint","IMPRINT",EDGE,{"derivedFrom":sQuery(id+"F6.wireOp",EDGE,"E14.0.15.0")}),1.0]])]});
            var Q18;
            Q18=makeQuery(id+"F6.imprint","IMPRINT",FACE,{"disambiguationData":[TD([[makeQuery(id+"F6.imprint","IMPRINT",EDGE,{"derivedFrom":sQuery(id+"F6.wireOp",EDGE,"E14.0.14.0")}),1.0]])]});
            var Q19;
            Q19=makeQuery(id+"F6.imprint","IMPRINT",FACE,{"disambiguationData":[TD([[makeQuery(id+"F6.imprint","IMPRINT",EDGE,{"derivedFrom":sQuery(id+"F6.wireOp",EDGE,"E14.0.13.0")}),1.0]])]});
            var Q20;
            Q20=makeQuery(id+"F6.imprint","IMPRINT",FACE,{"disambiguationData":[TD([[makeQuery(id+"F6.imprint","IMPRINT",EDGE,{"derivedFrom":sQuery(id+"F6.wireOp",EDGE,"E14.0.12.0")}),1.0]])]});
            var Q21;
            Q21=makeQuery(id+"F6.imprint","IMPRINT",FACE,{"disambiguationData":[TD([[makeQuery(id+"F6.imprint","IMPRINT",EDGE,{"derivedFrom":sQuery(id+"F6.wireOp",EDGE,"E14.0.3.0")}),1.0]])]});
            var Q22;
            Q22=makeQuery(id+"F6.imprint","IMPRINT",FACE,{"disambiguationData":[TD([[makeQuery(id+"F6.imprint","IMPRINT",EDGE,{"derivedFrom":sQuery(id+"F6.wireOp",EDGE,"E14.0.2.0")}),1.0]])]});
            var Q23;
            Q23=makeQuery(id+"F6.imprint","IMPRINT",FACE,{"disambiguationData":[TD([[makeQuery(id+"F6.imprint","IMPRINT",EDGE,{"derivedFrom":sQuery(id+"F6.wireOp",EDGE,"E14.0.4.0")}),1.0]])]});
            var Q24;
            Q24=makeQuery(id+"F6.imprint","IMPRINT",FACE,{"disambiguationData":[TD([[makeQuery(id+"F6.imprint","IMPRINT",EDGE,{"derivedFrom":sQuery(id+"F6.wireOp",EDGE,"E14.0.5.0")}),1.0]])]});
            var Q25;
            Q25=makeQuery(id+"F6.imprint","IMPRINT",FACE,{"disambiguationData":[TD([[makeQuery(id+"F6.imprint","IMPRINT",EDGE,{"derivedFrom":sQuery(id+"F6.wireOp",EDGE,"E14.0.6.0")}),1.0]])]});
            var Q26;
            Q26=makeQuery(id+"F6.imprint","IMPRINT",FACE,{"disambiguationData":[TD([[makeQuery(id+"F6.imprint","IMPRINT",EDGE,{"derivedFrom":sQuery(id+"F6.wireOp",EDGE,"E14.0.7.0")}),1.0]])]});
            var Q27;
            Q27=makeQuery(id+"F6.imprint","IMPRINT",FACE,{"disambiguationData":[TD([[makeQuery(id+"F6.imprint","IMPRINT",EDGE,{"derivedFrom":sQuery(id+"F6.wireOp",EDGE,"E14.0.8.0")}),1.0]])]});
            var Q28;
            Q28=makeQuery(id+"F6.imprint","IMPRINT",FACE,{"disambiguationData":[TD([[makeQuery(id+"F6.imprint","IMPRINT",EDGE,{"derivedFrom":sQuery(id+"F6.wireOp",EDGE,"E14.0.9.0")}),1.0]])]});
            var Q29;
            Q29=makeQuery(id+"F6.imprint","IMPRINT",FACE,{"disambiguationData":[TD([[makeQuery(id+"F6.imprint","IMPRINT",EDGE,{"derivedFrom":sQuery(id+"F6.wireOp",EDGE,"E14.0.10.0")}),1.0]])]});
            var Q30;
            Q30=makeQuery(id+"F6.imprint","IMPRINT",FACE,{"disambiguationData":[TD([[makeQuery(id+"F6.imprint","IMPRINT",EDGE,{"derivedFrom":sQuery(id+"F6.wireOp",EDGE,"E14.0.1.0")}),1.0]])]});
            var Q31;
            Q31=makeQuery(id+"F6.imprint","IMPRINT",FACE,{"disambiguationData":[TD([[makeQuery(id+"F6.imprint","IMPRINT",EDGE,{"derivedFrom":sQuery(id+"F6.wireOp",EDGE,"E13")}),1.0]])]});
            var Q32;
            Q32=makeQuery(id+"F6.imprint","IMPRINT",FACE,{"disambiguationData":[TD([[makeQuery(id+"F6.imprint","IMPRINT",EDGE,{"derivedFrom":sQuery(id+"F6.wireOp",EDGE,"E9.bottom")}),-1.0]])]});
            extrude(context, id + "F34", {"entities" : qUnion([Q0, Q1, Q2, Q3, Q4, Q5, Q6, Q7, Q8, Q9, Q10, Q11, Q12, Q13, Q14, Q15, Q16, Q17, Q18, Q19, Q20, Q21, Q22, Q23, Q24, Q25, Q26, Q27, Q28, Q29, Q30, Q31, Q32]), "depth" : 18.26 * mm});
        }
        {
            var Q0;
            Q0=makeQuery(id+"F34.opExtrude","SWEPT_BODY",BODY,{"disambiguationData":[OSD([sQuery(id+"F6.wireOp",EDGE,"E9.bottom"),sQuery(id+"F6.wireOp",EDGE,"E9.top"),sQuery(id+"F6.wireOp",EDGE,"E9.left"),sQuery(id+"F6.wireOp",EDGE,"E9.right"),sQuery(id+"F6.wireOp",EDGE,"E10"),sQuery(id+"F6.wireOp",EDGE,"E11")])]});
            transform(context, id + "F35", {"entities" : qUnion([Q0]), "transformType" : TransformType.TRANSLATION_3D, "dx" : 0 * mm, "dy" : 0 * mm, "dz" : 1270 * mm, "makeCopy" : false});
        }
        {
            var Q0;
            Q0=makeQuery(id+"F6.imprint","IMPRINT",FACE,{"disambiguationData":[TD([[makeQuery(id+"F6.imprint","IMPRINT",EDGE,{"derivedFrom":sQuery(id+"F6.wireOp",EDGE,"E9.bottom")}),-1.0]])]});
            var Q1;
            Q1=makeQuery(id+"F6.imprint","IMPRINT",FACE,{"disambiguationData":[TD([[makeQuery(id+"F6.imprint","IMPRINT",EDGE,{"derivedFrom":sQuery(id+"F6.wireOp",EDGE,"E14.0.11.0")}),1.0]])]});
            var Q2;
            Q2=makeQuery(id+"F6.imprint","IMPRINT",FACE,{"disambiguationData":[TD([[makeQuery(id+"F6.imprint","IMPRINT",EDGE,{"derivedFrom":sQuery(id+"F6.wireOp",EDGE,"E14.0.15.0")}),1.0]])]});
            var Q3;
            Q3=makeQuery(id+"F6.imprint","IMPRINT",FACE,{"disambiguationData":[TD([[makeQuery(id+"F6.imprint","IMPRINT",EDGE,{"derivedFrom":sQuery(id+"F6.wireOp",EDGE,"E14.0.14.0")}),1.0]])]});
            var Q4;
            Q4=makeQuery(id+"F6.imprint","IMPRINT",FACE,{"disambiguationData":[TD([[makeQuery(id+"F6.imprint","IMPRINT",EDGE,{"derivedFrom":sQuery(id+"F6.wireOp",EDGE,"E14.0.13.0")}),1.0]])]});
            var Q5;
            Q5=makeQuery(id+"F6.imprint","IMPRINT",FACE,{"disambiguationData":[TD([[makeQuery(id+"F6.imprint","IMPRINT",EDGE,{"derivedFrom":sQuery(id+"F6.wireOp",EDGE,"E14.0.12.0")}),1.0]])]});
            var Q6;
            Q6=makeQuery(id+"F6.imprint","IMPRINT",FACE,{"disambiguationData":[TD([[makeQuery(id+"F6.imprint","IMPRINT",EDGE,{"derivedFrom":sQuery(id+"F6.wireOp",EDGE,"E14.0.3.0")}),1.0]])]});
            var Q7;
            Q7=makeQuery(id+"F6.imprint","IMPRINT",FACE,{"disambiguationData":[TD([[makeQuery(id+"F6.imprint","IMPRINT",EDGE,{"derivedFrom":sQuery(id+"F6.wireOp",EDGE,"E14.0.2.0")}),1.0]])]});
            var Q8;
            Q8=makeQuery(id+"F6.imprint","IMPRINT",FACE,{"disambiguationData":[TD([[makeQuery(id+"F6.imprint","IMPRINT",EDGE,{"derivedFrom":sQuery(id+"F6.wireOp",EDGE,"E14.0.4.0")}),1.0]])]});
            var Q9;
            Q9=makeQuery(id+"F6.imprint","IMPRINT",FACE,{"disambiguationData":[TD([[makeQuery(id+"F6.imprint","IMPRINT",EDGE,{"derivedFrom":sQuery(id+"F6.wireOp",EDGE,"E14.0.5.0")}),1.0]])]});
            var Q10;
            Q10=makeQuery(id+"F6.imprint","IMPRINT",FACE,{"disambiguationData":[TD([[makeQuery(id+"F6.imprint","IMPRINT",EDGE,{"derivedFrom":sQuery(id+"F6.wireOp",EDGE,"E14.0.6.0")}),1.0]])]});
            var Q11;
            Q11=makeQuery(id+"F6.imprint","IMPRINT",FACE,{"disambiguationData":[TD([[makeQuery(id+"F6.imprint","IMPRINT",EDGE,{"derivedFrom":sQuery(id+"F6.wireOp",EDGE,"E14.0.7.0")}),1.0]])]});
            var Q12;
            Q12=makeQuery(id+"F6.imprint","IMPRINT",FACE,{"disambiguationData":[TD([[makeQuery(id+"F6.imprint","IMPRINT",EDGE,{"derivedFrom":sQuery(id+"F6.wireOp",EDGE,"E14.0.8.0")}),1.0]])]});
            var Q13;
            Q13=makeQuery(id+"F6.imprint","IMPRINT",FACE,{"disambiguationData":[TD([[makeQuery(id+"F6.imprint","IMPRINT",EDGE,{"derivedFrom":sQuery(id+"F6.wireOp",EDGE,"E14.0.9.0")}),1.0]])]});
            var Q14;
            Q14=makeQuery(id+"F6.imprint","IMPRINT",FACE,{"disambiguationData":[TD([[makeQuery(id+"F6.imprint","IMPRINT",EDGE,{"derivedFrom":sQuery(id+"F6.wireOp",EDGE,"E14.0.10.0")}),1.0]])]});
            var Q15;
            Q15=makeQuery(id+"F6.imprint","IMPRINT",FACE,{"disambiguationData":[TD([[makeQuery(id+"F6.imprint","IMPRINT",EDGE,{"derivedFrom":sQuery(id+"F6.wireOp",EDGE,"E14.0.1.0")}),1.0]])]});
            var Q16;
            Q16=makeQuery(id+"F6.imprint","IMPRINT",FACE,{"disambiguationData":[TD([[makeQuery(id+"F6.imprint","IMPRINT",EDGE,{"derivedFrom":sQuery(id+"F6.wireOp",EDGE,"E13")}),1.0]])]});
            var Q17;
            Q17=makeQuery(id+"F6.imprint","IMPRINT",FACE,{"disambiguationData":[TD([[makeQuery(id+"F6.imprint","IMPRINT",EDGE,{"derivedFrom":sQuery(id+"F6.wireOp",EDGE,"E14.1.8.0")}),1.0]])]});
            var Q18;
            Q18=makeQuery(id+"F6.imprint","IMPRINT",FACE,{"disambiguationData":[TD([[makeQuery(id+"F6.imprint","IMPRINT",EDGE,{"derivedFrom":sQuery(id+"F6.wireOp",EDGE,"E14.1.7.0")}),1.0]])]});
            var Q19;
            Q19=makeQuery(id+"F6.imprint","IMPRINT",FACE,{"disambiguationData":[TD([[makeQuery(id+"F6.imprint","IMPRINT",EDGE,{"derivedFrom":sQuery(id+"F6.wireOp",EDGE,"E14.1.6.0")}),1.0]])]});
            var Q20;
            Q20=makeQuery(id+"F6.imprint","IMPRINT",FACE,{"disambiguationData":[TD([[makeQuery(id+"F6.imprint","IMPRINT",EDGE,{"derivedFrom":sQuery(id+"F6.wireOp",EDGE,"E14.1.4.0")}),1.0]])]});
            var Q21;
            Q21=makeQuery(id+"F6.imprint","IMPRINT",FACE,{"disambiguationData":[TD([[makeQuery(id+"F6.imprint","IMPRINT",EDGE,{"derivedFrom":sQuery(id+"F6.wireOp",EDGE,"E14.1.10.0")}),1.0]])]});
            var Q22;
            Q22=makeQuery(id+"F6.imprint","IMPRINT",FACE,{"disambiguationData":[TD([[makeQuery(id+"F6.imprint","IMPRINT",EDGE,{"derivedFrom":sQuery(id+"F6.wireOp",EDGE,"E14.1.2.0")}),1.0]])]});
            var Q23;
            Q23=makeQuery(id+"F6.imprint","IMPRINT",FACE,{"disambiguationData":[TD([[makeQuery(id+"F6.imprint","IMPRINT",EDGE,{"derivedFrom":sQuery(id+"F6.wireOp",EDGE,"E14.1.1.0")}),1.0]])]});
            var Q24;
            Q24=makeQuery(id+"F6.imprint","IMPRINT",FACE,{"disambiguationData":[TD([[makeQuery(id+"F6.imprint","IMPRINT",EDGE,{"derivedFrom":sQuery(id+"F6.wireOp",EDGE,"E14.1.14.0")}),1.0]])]});
            var Q25;
            Q25=makeQuery(id+"F6.imprint","IMPRINT",FACE,{"disambiguationData":[TD([[makeQuery(id+"F6.imprint","IMPRINT",EDGE,{"derivedFrom":sQuery(id+"F6.wireOp",EDGE,"E14.1.3.0")}),1.0]])]});
            var Q26;
            Q26=makeQuery(id+"F6.imprint","IMPRINT",FACE,{"disambiguationData":[TD([[makeQuery(id+"F6.imprint","IMPRINT",EDGE,{"derivedFrom":sQuery(id+"F6.wireOp",EDGE,"E14.1.11.0")}),1.0]])]});
            var Q27;
            Q27=makeQuery(id+"F6.imprint","IMPRINT",FACE,{"disambiguationData":[TD([[makeQuery(id+"F6.imprint","IMPRINT",EDGE,{"derivedFrom":sQuery(id+"F6.wireOp",EDGE,"E14.1.12.0")}),1.0]])]});
            var Q28;
            Q28=makeQuery(id+"F6.imprint","IMPRINT",FACE,{"disambiguationData":[TD([[makeQuery(id+"F6.imprint","IMPRINT",EDGE,{"derivedFrom":sQuery(id+"F6.wireOp",EDGE,"E14.1.15.0")}),1.0]])]});
            var Q29;
            Q29=makeQuery(id+"F6.imprint","IMPRINT",FACE,{"disambiguationData":[TD([[makeQuery(id+"F6.imprint","IMPRINT",EDGE,{"derivedFrom":sQuery(id+"F6.wireOp",EDGE,"E14.1.9.0")}),1.0]])]});
            var Q30;
            Q30=makeQuery(id+"F6.imprint","IMPRINT",FACE,{"disambiguationData":[TD([[makeQuery(id+"F6.imprint","IMPRINT",EDGE,{"derivedFrom":sQuery(id+"F6.wireOp",EDGE,"E14.1.5.0")}),1.0]])]});
            var Q31;
            Q31=makeQuery(id+"F6.imprint","IMPRINT",FACE,{"disambiguationData":[TD([[makeQuery(id+"F6.imprint","IMPRINT",EDGE,{"derivedFrom":sQuery(id+"F6.wireOp",EDGE,"E14.1.13.0")}),1.0]])]});
            var Q32;
            Q32=makeQuery(id+"F6.imprint","IMPRINT",FACE,{"disambiguationData":[TD([[makeQuery(id+"F6.imprint","IMPRINT",EDGE,{"derivedFrom":sQuery(id+"F6.wireOp",EDGE,"E14.1.0.0")}),1.0]])]});
            extrude(context, id + "F36", {"entities" : qUnion([Q0, Q1, Q2, Q3, Q4, Q5, Q6, Q7, Q8, Q9, Q10, Q11, Q12, Q13, Q14, Q15, Q16, Q17, Q18, Q19, Q20, Q21, Q22, Q23, Q24, Q25, Q26, Q27, Q28, Q29, Q30, Q31, Q32]), "depth" : 18.26 * mm});
        }
        {
            var Q0;
            Q0=makeQuery(id+"F6.imprint","IMPRINT",FACE,{"disambiguationData":[TD([[makeQuery(id+"F6.imprint","IMPRINT",EDGE,{"derivedFrom":sQuery(id+"F6.wireOp",EDGE,"E9.bottom")}),-1.0]])]});
            var Q1;
            Q1=makeQuery(id+"F6.imprint","IMPRINT",FACE,{"disambiguationData":[TD([[makeQuery(id+"F6.imprint","IMPRINT",EDGE,{"derivedFrom":sQuery(id+"F6.wireOp",EDGE,"E14.0.11.0")}),1.0]])]});
            var Q2;
            Q2=makeQuery(id+"F6.imprint","IMPRINT",FACE,{"disambiguationData":[TD([[makeQuery(id+"F6.imprint","IMPRINT",EDGE,{"derivedFrom":sQuery(id+"F6.wireOp",EDGE,"E14.0.15.0")}),1.0]])]});
            var Q3;
            Q3=makeQuery(id+"F6.imprint","IMPRINT",FACE,{"disambiguationData":[TD([[makeQuery(id+"F6.imprint","IMPRINT",EDGE,{"derivedFrom":sQuery(id+"F6.wireOp",EDGE,"E14.0.14.0")}),1.0]])]});
            var Q4;
            Q4=makeQuery(id+"F6.imprint","IMPRINT",FACE,{"disambiguationData":[TD([[makeQuery(id+"F6.imprint","IMPRINT",EDGE,{"derivedFrom":sQuery(id+"F6.wireOp",EDGE,"E14.0.13.0")}),1.0]])]});
            var Q5;
            Q5=makeQuery(id+"F6.imprint","IMPRINT",FACE,{"disambiguationData":[TD([[makeQuery(id+"F6.imprint","IMPRINT",EDGE,{"derivedFrom":sQuery(id+"F6.wireOp",EDGE,"E14.0.12.0")}),1.0]])]});
            var Q6;
            Q6=makeQuery(id+"F6.imprint","IMPRINT",FACE,{"disambiguationData":[TD([[makeQuery(id+"F6.imprint","IMPRINT",EDGE,{"derivedFrom":sQuery(id+"F6.wireOp",EDGE,"E14.0.3.0")}),1.0]])]});
            var Q7;
            Q7=makeQuery(id+"F6.imprint","IMPRINT",FACE,{"disambiguationData":[TD([[makeQuery(id+"F6.imprint","IMPRINT",EDGE,{"derivedFrom":sQuery(id+"F6.wireOp",EDGE,"E14.0.2.0")}),1.0]])]});
            var Q8;
            Q8=makeQuery(id+"F6.imprint","IMPRINT",FACE,{"disambiguationData":[TD([[makeQuery(id+"F6.imprint","IMPRINT",EDGE,{"derivedFrom":sQuery(id+"F6.wireOp",EDGE,"E14.0.4.0")}),1.0]])]});
            var Q9;
            Q9=makeQuery(id+"F6.imprint","IMPRINT",FACE,{"disambiguationData":[TD([[makeQuery(id+"F6.imprint","IMPRINT",EDGE,{"derivedFrom":sQuery(id+"F6.wireOp",EDGE,"E14.0.5.0")}),1.0]])]});
            var Q10;
            Q10=makeQuery(id+"F6.imprint","IMPRINT",FACE,{"disambiguationData":[TD([[makeQuery(id+"F6.imprint","IMPRINT",EDGE,{"derivedFrom":sQuery(id+"F6.wireOp",EDGE,"E14.0.6.0")}),1.0]])]});
            var Q11;
            Q11=makeQuery(id+"F6.imprint","IMPRINT",FACE,{"disambiguationData":[TD([[makeQuery(id+"F6.imprint","IMPRINT",EDGE,{"derivedFrom":sQuery(id+"F6.wireOp",EDGE,"E14.0.7.0")}),1.0]])]});
            var Q12;
            Q12=makeQuery(id+"F6.imprint","IMPRINT",FACE,{"disambiguationData":[TD([[makeQuery(id+"F6.imprint","IMPRINT",EDGE,{"derivedFrom":sQuery(id+"F6.wireOp",EDGE,"E14.0.8.0")}),1.0]])]});
            var Q13;
            Q13=makeQuery(id+"F6.imprint","IMPRINT",FACE,{"disambiguationData":[TD([[makeQuery(id+"F6.imprint","IMPRINT",EDGE,{"derivedFrom":sQuery(id+"F6.wireOp",EDGE,"E14.0.9.0")}),1.0]])]});
            var Q14;
            Q14=makeQuery(id+"F6.imprint","IMPRINT",FACE,{"disambiguationData":[TD([[makeQuery(id+"F6.imprint","IMPRINT",EDGE,{"derivedFrom":sQuery(id+"F6.wireOp",EDGE,"E14.0.10.0")}),1.0]])]});
            var Q15;
            Q15=makeQuery(id+"F6.imprint","IMPRINT",FACE,{"disambiguationData":[TD([[makeQuery(id+"F6.imprint","IMPRINT",EDGE,{"derivedFrom":sQuery(id+"F6.wireOp",EDGE,"E14.0.1.0")}),1.0]])]});
            var Q16;
            Q16=makeQuery(id+"F6.imprint","IMPRINT",FACE,{"disambiguationData":[TD([[makeQuery(id+"F6.imprint","IMPRINT",EDGE,{"derivedFrom":sQuery(id+"F6.wireOp",EDGE,"E13")}),1.0]])]});
            var Q17;
            Q17=makeQuery(id+"F6.imprint","IMPRINT",FACE,{"disambiguationData":[TD([[makeQuery(id+"F6.imprint","IMPRINT",EDGE,{"derivedFrom":sQuery(id+"F6.wireOp",EDGE,"E14.1.8.0")}),1.0]])]});
            var Q18;
            Q18=makeQuery(id+"F6.imprint","IMPRINT",FACE,{"disambiguationData":[TD([[makeQuery(id+"F6.imprint","IMPRINT",EDGE,{"derivedFrom":sQuery(id+"F6.wireOp",EDGE,"E14.1.7.0")}),1.0]])]});
            var Q19;
            Q19=makeQuery(id+"F6.imprint","IMPRINT",FACE,{"disambiguationData":[TD([[makeQuery(id+"F6.imprint","IMPRINT",EDGE,{"derivedFrom":sQuery(id+"F6.wireOp",EDGE,"E14.1.6.0")}),1.0]])]});
            var Q20;
            Q20=makeQuery(id+"F6.imprint","IMPRINT",FACE,{"disambiguationData":[TD([[makeQuery(id+"F6.imprint","IMPRINT",EDGE,{"derivedFrom":sQuery(id+"F6.wireOp",EDGE,"E14.1.4.0")}),1.0]])]});
            var Q21;
            Q21=makeQuery(id+"F6.imprint","IMPRINT",FACE,{"disambiguationData":[TD([[makeQuery(id+"F6.imprint","IMPRINT",EDGE,{"derivedFrom":sQuery(id+"F6.wireOp",EDGE,"E14.1.10.0")}),1.0]])]});
            var Q22;
            Q22=makeQuery(id+"F6.imprint","IMPRINT",FACE,{"disambiguationData":[TD([[makeQuery(id+"F6.imprint","IMPRINT",EDGE,{"derivedFrom":sQuery(id+"F6.wireOp",EDGE,"E14.1.2.0")}),1.0]])]});
            var Q23;
            Q23=makeQuery(id+"F6.imprint","IMPRINT",FACE,{"disambiguationData":[TD([[makeQuery(id+"F6.imprint","IMPRINT",EDGE,{"derivedFrom":sQuery(id+"F6.wireOp",EDGE,"E14.1.1.0")}),1.0]])]});
            var Q24;
            Q24=makeQuery(id+"F6.imprint","IMPRINT",FACE,{"disambiguationData":[TD([[makeQuery(id+"F6.imprint","IMPRINT",EDGE,{"derivedFrom":sQuery(id+"F6.wireOp",EDGE,"E14.1.14.0")}),1.0]])]});
            var Q25;
            Q25=makeQuery(id+"F6.imprint","IMPRINT",FACE,{"disambiguationData":[TD([[makeQuery(id+"F6.imprint","IMPRINT",EDGE,{"derivedFrom":sQuery(id+"F6.wireOp",EDGE,"E14.1.3.0")}),1.0]])]});
            var Q26;
            Q26=makeQuery(id+"F6.imprint","IMPRINT",FACE,{"disambiguationData":[TD([[makeQuery(id+"F6.imprint","IMPRINT",EDGE,{"derivedFrom":sQuery(id+"F6.wireOp",EDGE,"E14.1.11.0")}),1.0]])]});
            var Q27;
            Q27=makeQuery(id+"F6.imprint","IMPRINT",FACE,{"disambiguationData":[TD([[makeQuery(id+"F6.imprint","IMPRINT",EDGE,{"derivedFrom":sQuery(id+"F6.wireOp",EDGE,"E14.1.12.0")}),1.0]])]});
            var Q28;
            Q28=makeQuery(id+"F6.imprint","IMPRINT",FACE,{"disambiguationData":[TD([[makeQuery(id+"F6.imprint","IMPRINT",EDGE,{"derivedFrom":sQuery(id+"F6.wireOp",EDGE,"E14.1.15.0")}),1.0]])]});
            var Q29;
            Q29=makeQuery(id+"F6.imprint","IMPRINT",FACE,{"disambiguationData":[TD([[makeQuery(id+"F6.imprint","IMPRINT",EDGE,{"derivedFrom":sQuery(id+"F6.wireOp",EDGE,"E14.1.9.0")}),1.0]])]});
            var Q30;
            Q30=makeQuery(id+"F6.imprint","IMPRINT",FACE,{"disambiguationData":[TD([[makeQuery(id+"F6.imprint","IMPRINT",EDGE,{"derivedFrom":sQuery(id+"F6.wireOp",EDGE,"E14.1.5.0")}),1.0]])]});
            var Q31;
            Q31=makeQuery(id+"F6.imprint","IMPRINT",FACE,{"disambiguationData":[TD([[makeQuery(id+"F6.imprint","IMPRINT",EDGE,{"derivedFrom":sQuery(id+"F6.wireOp",EDGE,"E14.1.13.0")}),1.0]])]});
            var Q32;
            Q32=makeQuery(id+"F6.imprint","IMPRINT",FACE,{"disambiguationData":[TD([[makeQuery(id+"F6.imprint","IMPRINT",EDGE,{"derivedFrom":sQuery(id+"F6.wireOp",EDGE,"E14.1.0.0")}),1.0]])]});
            extrude(context, id + "F37", {"entities" : qUnion([Q0, Q1, Q2, Q3, Q4, Q5, Q6, Q7, Q8, Q9, Q10, Q11, Q12, Q13, Q14, Q15, Q16, Q17, Q18, Q19, Q20, Q21, Q22, Q23, Q24, Q25, Q26, Q27, Q28, Q29, Q30, Q31, Q32]), "operationType" : NewBodyOperationType.REMOVE, "oppositeDirection" : true, "depth" : 12.7 * mm});
        }
        {
            var Q0;
            Q0=makeQuery(id+"F6.imprint","IMPRINT",FACE,{"disambiguationData":[TD([[makeQuery(id+"F6.imprint","IMPRINT",EDGE,{"derivedFrom":sQuery(id+"F6.wireOp",EDGE,"E14.1.8.0")}),1.0]])]});
            var Q1;
            Q1=makeQuery(id+"F6.imprint","IMPRINT",FACE,{"disambiguationData":[TD([[makeQuery(id+"F6.imprint","IMPRINT",EDGE,{"derivedFrom":sQuery(id+"F6.wireOp",EDGE,"E14.1.7.0")}),1.0]])]});
            var Q2;
            Q2=makeQuery(id+"F6.imprint","IMPRINT",FACE,{"disambiguationData":[TD([[makeQuery(id+"F6.imprint","IMPRINT",EDGE,{"derivedFrom":sQuery(id+"F6.wireOp",EDGE,"E14.1.6.0")}),1.0]])]});
            var Q3;
            Q3=makeQuery(id+"F6.imprint","IMPRINT",FACE,{"disambiguationData":[TD([[makeQuery(id+"F6.imprint","IMPRINT",EDGE,{"derivedFrom":sQuery(id+"F6.wireOp",EDGE,"E14.1.4.0")}),1.0]])]});
            var Q4;
            Q4=makeQuery(id+"F6.imprint","IMPRINT",FACE,{"disambiguationData":[TD([[makeQuery(id+"F6.imprint","IMPRINT",EDGE,{"derivedFrom":sQuery(id+"F6.wireOp",EDGE,"E14.1.10.0")}),1.0]])]});
            var Q5;
            Q5=makeQuery(id+"F6.imprint","IMPRINT",FACE,{"disambiguationData":[TD([[makeQuery(id+"F6.imprint","IMPRINT",EDGE,{"derivedFrom":sQuery(id+"F6.wireOp",EDGE,"E14.1.2.0")}),1.0]])]});
            var Q6;
            Q6=makeQuery(id+"F6.imprint","IMPRINT",FACE,{"disambiguationData":[TD([[makeQuery(id+"F6.imprint","IMPRINT",EDGE,{"derivedFrom":sQuery(id+"F6.wireOp",EDGE,"E14.1.1.0")}),1.0]])]});
            var Q7;
            Q7=makeQuery(id+"F6.imprint","IMPRINT",FACE,{"disambiguationData":[TD([[makeQuery(id+"F6.imprint","IMPRINT",EDGE,{"derivedFrom":sQuery(id+"F6.wireOp",EDGE,"E14.1.14.0")}),1.0]])]});
            var Q8;
            Q8=makeQuery(id+"F6.imprint","IMPRINT",FACE,{"disambiguationData":[TD([[makeQuery(id+"F6.imprint","IMPRINT",EDGE,{"derivedFrom":sQuery(id+"F6.wireOp",EDGE,"E14.1.3.0")}),1.0]])]});
            var Q9;
            Q9=makeQuery(id+"F6.imprint","IMPRINT",FACE,{"disambiguationData":[TD([[makeQuery(id+"F6.imprint","IMPRINT",EDGE,{"derivedFrom":sQuery(id+"F6.wireOp",EDGE,"E14.1.11.0")}),1.0]])]});
            var Q10;
            Q10=makeQuery(id+"F6.imprint","IMPRINT",FACE,{"disambiguationData":[TD([[makeQuery(id+"F6.imprint","IMPRINT",EDGE,{"derivedFrom":sQuery(id+"F6.wireOp",EDGE,"E14.1.12.0")}),1.0]])]});
            var Q11;
            Q11=makeQuery(id+"F6.imprint","IMPRINT",FACE,{"disambiguationData":[TD([[makeQuery(id+"F6.imprint","IMPRINT",EDGE,{"derivedFrom":sQuery(id+"F6.wireOp",EDGE,"E14.1.15.0")}),1.0]])]});
            var Q12;
            Q12=makeQuery(id+"F6.imprint","IMPRINT",FACE,{"disambiguationData":[TD([[makeQuery(id+"F6.imprint","IMPRINT",EDGE,{"derivedFrom":sQuery(id+"F6.wireOp",EDGE,"E14.1.9.0")}),1.0]])]});
            var Q13;
            Q13=makeQuery(id+"F6.imprint","IMPRINT",FACE,{"disambiguationData":[TD([[makeQuery(id+"F6.imprint","IMPRINT",EDGE,{"derivedFrom":sQuery(id+"F6.wireOp",EDGE,"E14.1.5.0")}),1.0]])]});
            var Q14;
            Q14=makeQuery(id+"F6.imprint","IMPRINT",FACE,{"disambiguationData":[TD([[makeQuery(id+"F6.imprint","IMPRINT",EDGE,{"derivedFrom":sQuery(id+"F6.wireOp",EDGE,"E14.1.13.0")}),1.0]])]});
            var Q15;
            Q15=makeQuery(id+"F6.imprint","IMPRINT",FACE,{"disambiguationData":[TD([[makeQuery(id+"F6.imprint","IMPRINT",EDGE,{"derivedFrom":sQuery(id+"F6.wireOp",EDGE,"E14.1.0.0")}),1.0]])]});
            var Q16;
            Q16=makeQuery(id+"F6.imprint","IMPRINT",FACE,{"disambiguationData":[TD([[makeQuery(id+"F6.imprint","IMPRINT",EDGE,{"derivedFrom":sQuery(id+"F6.wireOp",EDGE,"E14.0.11.0")}),1.0]])]});
            var Q17;
            Q17=makeQuery(id+"F6.imprint","IMPRINT",FACE,{"disambiguationData":[TD([[makeQuery(id+"F6.imprint","IMPRINT",EDGE,{"derivedFrom":sQuery(id+"F6.wireOp",EDGE,"E14.0.15.0")}),1.0]])]});
            var Q18;
            Q18=makeQuery(id+"F6.imprint","IMPRINT",FACE,{"disambiguationData":[TD([[makeQuery(id+"F6.imprint","IMPRINT",EDGE,{"derivedFrom":sQuery(id+"F6.wireOp",EDGE,"E14.0.14.0")}),1.0]])]});
            var Q19;
            Q19=makeQuery(id+"F6.imprint","IMPRINT",FACE,{"disambiguationData":[TD([[makeQuery(id+"F6.imprint","IMPRINT",EDGE,{"derivedFrom":sQuery(id+"F6.wireOp",EDGE,"E14.0.13.0")}),1.0]])]});
            var Q20;
            Q20=makeQuery(id+"F6.imprint","IMPRINT",FACE,{"disambiguationData":[TD([[makeQuery(id+"F6.imprint","IMPRINT",EDGE,{"derivedFrom":sQuery(id+"F6.wireOp",EDGE,"E14.0.12.0")}),1.0]])]});
            var Q21;
            Q21=makeQuery(id+"F6.imprint","IMPRINT",FACE,{"disambiguationData":[TD([[makeQuery(id+"F6.imprint","IMPRINT",EDGE,{"derivedFrom":sQuery(id+"F6.wireOp",EDGE,"E14.0.3.0")}),1.0]])]});
            var Q22;
            Q22=makeQuery(id+"F6.imprint","IMPRINT",FACE,{"disambiguationData":[TD([[makeQuery(id+"F6.imprint","IMPRINT",EDGE,{"derivedFrom":sQuery(id+"F6.wireOp",EDGE,"E14.0.2.0")}),1.0]])]});
            var Q23;
            Q23=makeQuery(id+"F6.imprint","IMPRINT",FACE,{"disambiguationData":[TD([[makeQuery(id+"F6.imprint","IMPRINT",EDGE,{"derivedFrom":sQuery(id+"F6.wireOp",EDGE,"E14.0.4.0")}),1.0]])]});
            var Q24;
            Q24=makeQuery(id+"F6.imprint","IMPRINT",FACE,{"disambiguationData":[TD([[makeQuery(id+"F6.imprint","IMPRINT",EDGE,{"derivedFrom":sQuery(id+"F6.wireOp",EDGE,"E14.0.5.0")}),1.0]])]});
            var Q25;
            Q25=makeQuery(id+"F6.imprint","IMPRINT",FACE,{"disambiguationData":[TD([[makeQuery(id+"F6.imprint","IMPRINT",EDGE,{"derivedFrom":sQuery(id+"F6.wireOp",EDGE,"E14.0.6.0")}),1.0]])]});
            var Q26;
            Q26=makeQuery(id+"F6.imprint","IMPRINT",FACE,{"disambiguationData":[TD([[makeQuery(id+"F6.imprint","IMPRINT",EDGE,{"derivedFrom":sQuery(id+"F6.wireOp",EDGE,"E14.0.7.0")}),1.0]])]});
            var Q27;
            Q27=makeQuery(id+"F6.imprint","IMPRINT",FACE,{"disambiguationData":[TD([[makeQuery(id+"F6.imprint","IMPRINT",EDGE,{"derivedFrom":sQuery(id+"F6.wireOp",EDGE,"E14.0.8.0")}),1.0]])]});
            var Q28;
            Q28=makeQuery(id+"F6.imprint","IMPRINT",FACE,{"disambiguationData":[TD([[makeQuery(id+"F6.imprint","IMPRINT",EDGE,{"derivedFrom":sQuery(id+"F6.wireOp",EDGE,"E14.0.9.0")}),1.0]])]});
            var Q29;
            Q29=makeQuery(id+"F6.imprint","IMPRINT",FACE,{"disambiguationData":[TD([[makeQuery(id+"F6.imprint","IMPRINT",EDGE,{"derivedFrom":sQuery(id+"F6.wireOp",EDGE,"E14.0.10.0")}),1.0]])]});
            var Q30;
            Q30=makeQuery(id+"F6.imprint","IMPRINT",FACE,{"disambiguationData":[TD([[makeQuery(id+"F6.imprint","IMPRINT",EDGE,{"derivedFrom":sQuery(id+"F6.wireOp",EDGE,"E14.0.1.0")}),1.0]])]});
            var Q31;
            Q31=makeQuery(id+"F6.imprint","IMPRINT",FACE,{"disambiguationData":[TD([[makeQuery(id+"F6.imprint","IMPRINT",EDGE,{"derivedFrom":sQuery(id+"F6.wireOp",EDGE,"E13")}),1.0]])]});
            extrude(context, id + "F38", {"entities" : qUnion([Q0, Q1, Q2, Q3, Q4, Q5, Q6, Q7, Q8, Q9, Q10, Q11, Q12, Q13, Q14, Q15, Q16, Q17, Q18, Q19, Q20, Q21, Q22, Q23, Q24, Q25, Q26, Q27, Q28, Q29, Q30, Q31]), "operationType" : NewBodyOperationType.REMOVE, "depth" : 12.7 * mm});
        }
        {
            var Q0;
            Q0=makeQuery(id+"F34.opExtrude","SWEPT_BODY",BODY,{"disambiguationData":[OSD([sQuery(id+"F6.wireOp",EDGE,"E9.bottom"),sQuery(id+"F6.wireOp",EDGE,"E9.top"),sQuery(id+"F6.wireOp",EDGE,"E9.left"),sQuery(id+"F6.wireOp",EDGE,"E9.right"),sQuery(id+"F6.wireOp",EDGE,"E10"),sQuery(id+"F6.wireOp",EDGE,"E11")])]});
            deleteBodies(context, id + "F39", {"entities" : qUnion([Q0])});
        }
        {
            var Q0;
            Q0=makeQuery(id+"F8.opPattern","COPY",BODY,{"derivedFrom":makeQuery(id+"F7.opExtrude","SWEPT_BODY",BODY,{"disambiguationData":[OSD([sQuery(id+"F6.wireOp",EDGE,"E9.bottom"),sQuery(id+"F6.wireOp",EDGE,"E9.top"),sQuery(id+"F6.wireOp",EDGE,"E9.left"),sQuery(id+"F6.wireOp",EDGE,"E9.right"),sQuery(id+"F6.wireOp",EDGE,"E10"),sQuery(id+"F6.wireOp",EDGE,"E11"),sQuery(id+"F6.wireOp",EDGE,"E13"),sQuery(id+"F6.wireOp",EDGE,"E14.0.1.0"),sQuery(id+"F6.wireOp",EDGE,"E14.0.2.0"),sQuery(id+"F6.wireOp",EDGE,"E14.0.3.0"),sQuery(id+"F6.wireOp",EDGE,"E14.0.4.0"),sQuery(id+"F6.wireOp",EDGE,"E14.0.5.0"),sQuery(id+"F6.wireOp",EDGE,"E14.0.6.0"),sQuery(id+"F6.wireOp",EDGE,"E14.0.7.0"),sQuery(id+"F6.wireOp",EDGE,"E14.0.8.0"),sQuery(id+"F6.wireOp",EDGE,"E14.0.9.0"),sQuery(id+"F6.wireOp",EDGE,"E14.0.10.0"),sQuery(id+"F6.wireOp",EDGE,"E14.0.11.0"),sQuery(id+"F6.wireOp",EDGE,"E14.0.12.0"),sQuery(id+"F6.wireOp",EDGE,"E14.0.13.0"),sQuery(id+"F6.wireOp",EDGE,"E14.0.14.0"),sQuery(id+"F6.wireOp",EDGE,"E14.0.15.0"),sQuery(id+"F6.wireOp",EDGE,"E14.1.0.0"),sQuery(id+"F6.wireOp",EDGE,"E14.1.1.0"),sQuery(id+"F6.wireOp",EDGE,"E14.1.2.0"),sQuery(id+"F6.wireOp",EDGE,"E14.1.3.0"),sQuery(id+"F6.wireOp",EDGE,"E14.1.4.0"),sQuery(id+"F6.wireOp",EDGE,"E14.1.5.0"),sQuery(id+"F6.wireOp",EDGE,"E14.1.6.0"),sQuery(id+"F6.wireOp",EDGE,"E14.1.7.0"),sQuery(id+"F6.wireOp",EDGE,"E14.1.8.0"),sQuery(id+"F6.wireOp",EDGE,"E14.1.9.0"),sQuery(id+"F6.wireOp",EDGE,"E14.1.10.0"),sQuery(id+"F6.wireOp",EDGE,"E14.1.11.0"),sQuery(id+"F6.wireOp",EDGE,"E14.1.12.0"),sQuery(id+"F6.wireOp",EDGE,"E14.1.13.0"),sQuery(id+"F6.wireOp",EDGE,"E14.1.14.0"),sQuery(id+"F6.wireOp",EDGE,"E14.1.15.0")])]}),"instanceName":"1"});
            deleteBodies(context, id + "F40", {"entities" : qUnion([Q0])});
        }
        {
            var Q0;
            Q0=makeQuery(id+"F36.opExtrude","SWEPT_BODY",BODY,{"disambiguationData":[OSD([sQuery(id+"F6.wireOp",EDGE,"E9.bottom"),sQuery(id+"F6.wireOp",EDGE,"E9.top"),sQuery(id+"F6.wireOp",EDGE,"E9.left"),sQuery(id+"F6.wireOp",EDGE,"E9.right"),sQuery(id+"F6.wireOp",EDGE,"E10"),sQuery(id+"F6.wireOp",EDGE,"E11")])]});
            transform(context, id + "F41", {"entities" : qUnion([Q0]), "transformType" : TransformType.TRANSLATION_3D, "dx" : 0 * mm, "dy" : 0 * mm, "dz" : 1270 * mm, "makeCopy" : false});
        }
        {
            var Q0;
            Q0=makeQuery(id+"F6.imprint","IMPRINT",FACE,{"disambiguationData":[TD([[makeQuery(id+"F6.imprint","IMPRINT",EDGE,{"derivedFrom":sQuery(id+"F6.wireOp",EDGE,"E9.bottom")}),-1.0]])]});
            var Q1;
            Q1=makeQuery(id+"F6.imprint","IMPRINT",FACE,{"disambiguationData":[TD([[makeQuery(id+"F6.imprint","IMPRINT",EDGE,{"derivedFrom":sQuery(id+"F6.wireOp",EDGE,"E11")}),1.0]])]});
            var Q2;
            Q2=makeQuery(id+"F6.imprint","IMPRINT",FACE,{"disambiguationData":[TD([[makeQuery(id+"F6.imprint","IMPRINT",EDGE,{"derivedFrom":sQuery(id+"F6.wireOp",EDGE,"E10")}),1.0]])]});
            extrude(context, id + "F42", {"entities" : qUnion([Q0, Q1, Q2]), "depth" : 18.26 * mm});
        }
        {
            var Q0;
            Q0=makeQuery(id+"F27.opExtrude","SWEPT_BODY",BODY,{"disambiguationData":[OSD([sQuery(id+"F26.wireOp",EDGE,"E18.bottom"),sQuery(id+"F26.wireOp",EDGE,"E18.top"),sQuery(id+"F26.wireOp",EDGE,"E18.left"),sQuery(id+"F26.wireOp",EDGE,"E18.right"),sQuery(id+"F26.wireOp",EDGE,"E19.filletArc"),sQuery(id+"F26.wireOp",EDGE,"E20.filletArc"),sQuery(id+"F26.wireOp",EDGE,"E27")])]});
            var Q1;
            Q1=makeQuery(id+"F27.opExtrude","SWEPT_FACE",FACE,{"disambiguationData":[OSD([sQuery(id+"F26.wireOp",EDGE,"E18.left")])]});
            mirror(context, id + "F43", {"entities" : qUnion([Q0]), "mirrorPlane" : qUnion([Q1])});
        }
        {
            var Q0;
            Q0=makeQuery(id+"F5.opExtrude","CAP_FACE",FACE,{"disambiguationData":[OSD([sQuery(id+"F4.wireOp",EDGE,"E8.bottom"),sQuery(id+"F4.wireOp",EDGE,"E8.top"),sQuery(id+"F4.wireOp",EDGE,"E8.left"),sQuery(id+"F4.wireOp",EDGE,"E8.right")])],"isStart":true});
            var sketch = newSketch(context, id + "F44", { "sketchPlane" : qUnion([Q0])});
            skPoint(sketch, "E31", {"position": v(-2669.25, -292.58) * mm});
            skPoint(sketch, "E32.0.1.0", {"position": v(-2669.25, -165.58) * mm});
            skPoint(sketch, "E32.0.2.0", {"position": v(-2669.25, -38.58) * mm});
            skPoint(sketch, "E32.0.3.0", {"position": v(-2669.25, 88.42) * mm});
            skPoint(sketch, "E32.0.4.0", {"position": v(-2669.25, 215.42) * mm});
            skPoint(sketch, "E32.0.5.0", {"position": v(-2669.25, 342.42) * mm});
            skPoint(sketch, "E32.0.6.0", {"position": v(-2669.25, 469.42) * mm});
            skPoint(sketch, "E32.1.0.0", {"position": v(-1773.12, -292.58) * mm});
            skPoint(sketch, "E32.1.1.0", {"position": v(-1773.12, -165.58) * mm});
            skPoint(sketch, "E32.1.2.0", {"position": v(-1773.12, -38.58) * mm});
            skPoint(sketch, "E32.1.3.0", {"position": v(-1773.12, 88.42) * mm});
            skPoint(sketch, "E32.1.4.0", {"position": v(-1773.12, 215.42) * mm});
            skPoint(sketch, "E32.1.5.0", {"position": v(-1773.12, 342.42) * mm});
            skPoint(sketch, "E32.1.6.0", {"position": v(-1773.12, 469.42) * mm});
            skLineSegment(sketch, "E32.direction1", {"start": v(-2669.25, -292.58) * mm, "end": v(-1773.12, -292.58) * mm, "construction": true});
            skLineSegment(sketch, "E32.direction2", {"start": v(-2669.25, -292.58) * mm, "end": v(-2669.25, -165.58) * mm, "construction": true});
            skSolve(sketch);
        }
        {
            var Q0;
            Q0=sQuery(id+"F44.wireOp",VERTEX,"E32.0.6.0");
            var Q1;
            Q1=sQuery(id+"F44.wireOp",VERTEX,"E32.0.5.0");
            var Q2;
            Q2=sQuery(id+"F44.wireOp",VERTEX,"E32.0.4.0");
            var Q3;
            Q3=sQuery(id+"F44.wireOp",VERTEX,"E32.0.3.0");
            var Q4;
            Q4=sQuery(id+"F44.wireOp",VERTEX,"E32.0.2.0");
            var Q5;
            Q5=sQuery(id+"F44.wireOp",VERTEX,"E32.0.1.0");
            var Q6;
            Q6=sQuery(id+"F44.wireOp",VERTEX,"E31");
            var Q7;
            Q7=sQuery(id+"F44.wireOp",VERTEX,"E32.1.0.0");
            var Q8;
            Q8=sQuery(id+"F44.wireOp",VERTEX,"E32.1.1.0");
            var Q9;
            Q9=sQuery(id+"F44.wireOp",VERTEX,"E32.1.2.0");
            var Q10;
            Q10=sQuery(id+"F44.wireOp",VERTEX,"E32.1.3.0");
            var Q11;
            Q11=sQuery(id+"F44.wireOp",VERTEX,"E32.1.4.0");
            var Q12;
            Q12=sQuery(id+"F44.wireOp",VERTEX,"E32.1.5.0");
            var Q13;
            Q13=sQuery(id+"F44.wireOp",VERTEX,"E32.1.6.0");
            var Q14;
            Q14=makeQuery(id+"F5.opExtrude","SWEPT_BODY",BODY,{"disambiguationData":[OSD([sQuery(id+"F4.wireOp",EDGE,"E8.bottom"),sQuery(id+"F4.wireOp",EDGE,"E8.top"),sQuery(id+"F4.wireOp",EDGE,"E8.left"),sQuery(id+"F4.wireOp",EDGE,"E8.right")])]});
            hole(context, id + "F45", {"style" : HoleStyle.C_SINK, "endStyle" : HoleEndStyle.THROUGH, "holeDiameter" : 3.97 * mm, "cSinkDiameter" : 8.73 * mm, "cSinkAngle" : 90 * degree, "locations" : qUnion([Q0, Q1, Q2, Q3, Q4, Q5, Q6, Q7, Q8, Q9, Q10, Q11, Q12, Q13]), "scope" : qUnion([Q14]), "isTappedThrough" : true, "startStyle" : HoleStartStyle.PART});
        }
        {
            var Q0;
            Q0=makeQuery(id+"F3.opExtrude","CAP_FACE",FACE,{"disambiguationData":[OSD([sQuery(id+"F2.wireOp",EDGE,"E7.bottom"),sQuery(id+"F2.wireOp",EDGE,"E7.top"),sQuery(id+"F2.wireOp",EDGE,"E7.left"),sQuery(id+"F2.wireOp",EDGE,"E7.right")])],"isStart":true});
            var sketch = newSketch(context, id + "F46", { "sketchPlane" : qUnion([Q0])});
            skPoint(sketch, "E33", {"position": v(-1288.16, -69.65) * mm});
            skPoint(sketch, "E34.0.1.0", {"position": v(-1288.16, 57.35) * mm});
            skPoint(sketch, "E34.0.2.0", {"position": v(-1288.16, 184.35) * mm});
            skPoint(sketch, "E34.0.3.0", {"position": v(-1288.16, 311.35) * mm});
            skPoint(sketch, "E34.0.4.0", {"position": v(-1288.16, 438.35) * mm});
            skPoint(sketch, "E34.1.0.0", {"position": v(-392.02, -69.65) * mm});
            skPoint(sketch, "E34.1.1.0", {"position": v(-392.02, 57.35) * mm});
            skPoint(sketch, "E34.1.2.0", {"position": v(-392.02, 184.35) * mm});
            skPoint(sketch, "E34.1.3.0", {"position": v(-392.02, 311.35) * mm});
            skPoint(sketch, "E34.1.4.0", {"position": v(-392.02, 438.35) * mm});
            skLineSegment(sketch, "E34.direction1", {"start": v(-1288.16, -69.65) * mm, "end": v(-392.02, -69.65) * mm, "construction": true});
            skLineSegment(sketch, "E34.direction2", {"start": v(-1288.16, -69.65) * mm, "end": v(-1288.16, 57.35) * mm, "construction": true});
            skPoint(sketch, "E35.3.0.0", {"position": v(-840.08, -111.32) * mm});
            skPoint(sketch, "E36", {"position": v(-840.08, -69.65) * mm});
            skPoint(sketch, "E37.0.1.0", {"position": v(-840.08, 57.35) * mm});
            skPoint(sketch, "E37.0.2.0", {"position": v(-840.08, 184.35) * mm});
            skPoint(sketch, "E37.0.3.0", {"position": v(-840.08, 311.35) * mm});
            skPoint(sketch, "E37.0.4.0", {"position": v(-840.08, 438.35) * mm});
            skLineSegment(sketch, "E37.direction1", {"start": v(-976.17, -69.65) * mm, "end": v(-840.08, -69.65) * mm, "construction": true});
            skLineSegment(sketch, "E37.direction2", {"start": v(-840.08, -69.65) * mm, "end": v(-840.08, 57.35) * mm, "construction": true});
            skPoint(sketch, "E38.positionSnap0", {"position": v(-1221.08, 184.35) * mm});
            skPoint(sketch, "E39", {"position": v(-840.08, 480.02) * mm});
            skPoint(sketch, "E40", {"position": v(-1052.8, -111.32) * mm});
            skPoint(sketch, "E41", {"position": v(-627.36, -111.32) * mm});
            skPoint(sketch, "E42", {"position": v(-1179.8, -111.32) * mm});
            skPoint(sketch, "E43", {"position": v(-754.36, -111.32) * mm});
            skPoint(sketch, "E44.2.0.0", {"position": v(-925.8, -111.32) * mm});
            skPoint(sketch, "E45.2.0.0", {"position": v(-500.36, -111.32) * mm});
            skPoint(sketch, "E46", {"position": v(-1287.76, -111.32) * mm});
            skPoint(sketch, "E47.1.0.0", {"position": v(-1243.3, -111.32) * mm});
            skPoint(sketch, "E48", {"position": v(-862.3, -111.32) * mm});
            skPoint(sketch, "E49", {"position": v(-436.86, -111.32) * mm});
            skPoint(sketch, "E50.1.0.0", {"position": v(-817.86, -111.32) * mm});
            skPoint(sketch, "E51.1.0.0", {"position": v(-392.4, -111.32) * mm});
            skPoint(sketch, "E52", {"position": v(-1221.08, 480.02) * mm});
            skPoint(sketch, "E53.1.0.0", {"position": v(-1094.08, 480.02) * mm});
            skPoint(sketch, "E53.2.0.0", {"position": v(-967.08, 480.02) * mm});
            skPoint(sketch, "E53.4.0.0", {"position": v(-713.08, 480.02) * mm});
            skPoint(sketch, "E53.5.0.0", {"position": v(-586.08, 480.02) * mm});
            skPoint(sketch, "E53.6.0.0", {"position": v(-459.08, 480.02) * mm});
            skPoint(sketch, "E54", {"position": v(-382.88, 489.15) * mm});
            skSolve(sketch);
        }
        {
            var Q0;
            Q0=sQuery(id+"F46.wireOp",VERTEX,"E34.0.4.0");
            var Q1;
            Q1=sQuery(id+"F46.wireOp",VERTEX,"E34.0.3.0");
            var Q2;
            Q2=sQuery(id+"F46.wireOp",VERTEX,"E34.0.2.0");
            var Q3;
            Q3=sQuery(id+"F46.wireOp",VERTEX,"E34.0.1.0");
            var Q4;
            Q4=sQuery(id+"F46.wireOp",VERTEX,"E33");
            var Q5;
            Q5=sQuery(id+"F46.wireOp",VERTEX,"E34.1.0.0");
            var Q6;
            Q6=sQuery(id+"F46.wireOp",VERTEX,"E34.1.2.0");
            var Q7;
            Q7=sQuery(id+"F46.wireOp",VERTEX,"E34.1.3.0");
            var Q8;
            Q8=sQuery(id+"F46.wireOp",VERTEX,"E34.1.4.0");
            var Q9;
            Q9=sQuery(id+"F46.wireOp",VERTEX,"E34.1.1.0");
            var Q10;
            Q10=makeQuery(id+"F3.opExtrude","SWEPT_BODY",BODY,{"disambiguationData":[OSD([sQuery(id+"F2.wireOp",EDGE,"E7.bottom"),sQuery(id+"F2.wireOp",EDGE,"E7.top"),sQuery(id+"F2.wireOp",EDGE,"E7.left"),sQuery(id+"F2.wireOp",EDGE,"E7.right")])]});
            hole(context, id + "F47", {"style" : HoleStyle.C_SINK, "endStyle" : HoleEndStyle.THROUGH, "holeDiameter" : 3.97 * mm, "cSinkDiameter" : 8.73 * mm, "cSinkAngle" : 90 * degree, "locations" : qUnion([Q0, Q1, Q2, Q3, Q4, Q5, Q6, Q7, Q8, Q9]), "scope" : qUnion([Q10]), "isTappedThrough" : true, "startStyle" : HoleStartStyle.PART});
        }
        {
            var Q0;
            Q0=sQuery(id+"F46.wireOp",VERTEX,"E37.0.4.0");
            var Q1;
            Q1=sQuery(id+"F46.wireOp",VERTEX,"E37.0.3.0");
            var Q2;
            Q2=sQuery(id+"F46.wireOp",VERTEX,"E37.0.2.0");
            var Q3;
            Q3=sQuery(id+"F46.wireOp",VERTEX,"E37.0.1.0");
            var Q4;
            Q4=sQuery(id+"F46.wireOp",VERTEX,"E36");
            var Q5;
            Q5=makeQuery(id+"F3.opExtrude","SWEPT_BODY",BODY,{"disambiguationData":[OSD([sQuery(id+"F2.wireOp",EDGE,"E7.bottom"),sQuery(id+"F2.wireOp",EDGE,"E7.top"),sQuery(id+"F2.wireOp",EDGE,"E7.left"),sQuery(id+"F2.wireOp",EDGE,"E7.right")])]});
            hole(context, id + "F48", {"style" : HoleStyle.C_SINK, "endStyle" : HoleEndStyle.THROUGH, "holeDiameter" : 3.97 * mm, "cSinkDiameter" : 8.73 * mm, "cSinkAngle" : 90 * degree, "locations" : qUnion([Q0, Q1, Q2, Q3, Q4]), "scope" : qUnion([Q5]), "isTappedThrough" : true, "startStyle" : HoleStartStyle.PART});
        }
        {
            var Q0;
            Q0=makeQuery(id+"F22.opExtrude","CAP_FACE",FACE,{"disambiguationData":[OSD([sQuery(id+"F21.wireOp",EDGE,"E17.bottom"),sQuery(id+"F21.wireOp",EDGE,"E17.top"),sQuery(id+"F21.wireOp",EDGE,"E17.left"),sQuery(id+"F21.wireOp",EDGE,"E17.right")])],"isStart":true});
            var sketch = newSketch(context, id + "F49", { "sketchPlane" : qUnion([Q0])});
            skLineSegment(sketch, "E55.bottom", {"start": v(-5753.49, 1553.44) * mm, "end": v(-5143.89, 1553.44) * mm});
            skLineSegment(sketch, "E55.top", {"start": v(-5753.49, 639.04) * mm, "end": v(-5143.89, 639.04) * mm});
            skLineSegment(sketch, "E55.left", {"start": v(-5753.49, 1553.44) * mm, "end": v(-5753.49, 639.04) * mm});
            skLineSegment(sketch, "E55.right", {"start": v(-5143.89, 1553.44) * mm, "end": v(-5143.89, 639.04) * mm});
            skPoint(sketch, "E56", {"position": v(-5816.99, 575.54) * mm});
            skPoint(sketch, "E57", {"position": v(-5702.69, 1096.24) * mm});
            skPoint(sketch, "E58.1.0.0", {"position": v(-5575.69, 1096.24) * mm});
            skPoint(sketch, "E58.2.0.0", {"position": v(-5448.69, 1096.24) * mm});
            skPoint(sketch, "E58.3.0.0", {"position": v(-5321.69, 1096.24) * mm});
            skPoint(sketch, "E58.4.0.0", {"position": v(-5194.69, 1096.24) * mm});
            skLineSegment(sketch, "E58.direction1", {"start": v(-5702.69, 1096.24) * mm, "end": v(-5575.69, 1096.24) * mm, "construction": true});
            skPoint(sketch, "E59", {"position": v(-5702.69, 1544.3) * mm});
            skPoint(sketch, "E60.1.0.0", {"position": v(-5575.69, 1544.3) * mm});
            skPoint(sketch, "E60.2.0.0", {"position": v(-5448.69, 1544.3) * mm});
            skPoint(sketch, "E60.3.0.0", {"position": v(-5321.69, 1544.3) * mm});
            skPoint(sketch, "E60.4.0.0", {"position": v(-5194.69, 1544.3) * mm});
            skLineSegment(sketch, "E60.direction1", {"start": v(-5702.69, 1544.3) * mm, "end": v(-5575.69, 1544.3) * mm, "construction": true});
            skPoint(sketch, "E61", {"position": v(-5702.69, 648.16) * mm});
            skPoint(sketch, "E62.1.0.0", {"position": v(-5575.69, 648.16) * mm});
            skPoint(sketch, "E62.2.0.0", {"position": v(-5448.69, 648.16) * mm});
            skPoint(sketch, "E62.3.0.0", {"position": v(-5321.69, 648.16) * mm});
            skPoint(sketch, "E62.4.0.0", {"position": v(-5194.69, 648.16) * mm});
            skLineSegment(sketch, "E62.direction1", {"start": v(-5702.69, 648.16) * mm, "end": v(-5575.69, 648.16) * mm, "construction": true});
            skPoint(sketch, "E63", {"position": v(-5744.35, 715.24) * mm});
            skPoint(sketch, "E64.0.1.0", {"position": v(-5744.35, 842.24) * mm});
            skPoint(sketch, "E64.0.2.0", {"position": v(-5744.35, 969.24) * mm});
            skPoint(sketch, "E64.0.3.0", {"position": v(-5744.35, 1096.24) * mm});
            skPoint(sketch, "E64.0.4.0", {"position": v(-5744.35, 1223.24) * mm});
            skPoint(sketch, "E64.0.5.0", {"position": v(-5744.35, 1350.24) * mm});
            skPoint(sketch, "E64.0.6.0", {"position": v(-5744.35, 1477.24) * mm});
            skLineSegment(sketch, "E64.direction1", {"start": v(-5744.35, 715.24) * mm, "end": v(-5153.01, 715.24) * mm, "construction": true});
            skLineSegment(sketch, "E64.direction2", {"start": v(-5744.35, 715.24) * mm, "end": v(-5744.35, 842.24) * mm, "construction": true});
            skLineSegment(sketch, "E65.bottom", {"start": v(-5162.94, 1553.44) * mm, "end": v(-5143.89, 1553.44) * mm});
            skLineSegment(sketch, "E65.top", {"start": v(-5162.94, 1489.94) * mm, "end": v(-5143.89, 1489.94) * mm});
            skLineSegment(sketch, "E65.left", {"start": v(-5162.94, 1553.44) * mm, "end": v(-5162.94, 1489.94) * mm});
            skLineSegment(sketch, "E65.right", {"start": v(-5143.89, 1553.44) * mm, "end": v(-5143.89, 1489.94) * mm});
            skLineSegment(sketch, "E66.bottom", {"start": v(-5162.94, 702.54) * mm, "end": v(-5143.89, 702.54) * mm});
            skLineSegment(sketch, "E66.top", {"start": v(-5162.94, 639.04) * mm, "end": v(-5143.89, 639.04) * mm});
            skLineSegment(sketch, "E66.left", {"start": v(-5162.94, 702.54) * mm, "end": v(-5162.94, 639.04) * mm});
            skLineSegment(sketch, "E66.right", {"start": v(-5143.89, 702.54) * mm, "end": v(-5143.89, 639.04) * mm});
            skLineSegment(sketch, "E67.bottom", {"start": v(-5162.94, 1127.99) * mm, "end": v(-5143.89, 1127.99) * mm});
            skLineSegment(sketch, "E67.top", {"start": v(-5162.94, 1064.49) * mm, "end": v(-5143.89, 1064.49) * mm});
            skLineSegment(sketch, "E67.left", {"start": v(-5162.94, 1127.99) * mm, "end": v(-5162.94, 1064.49) * mm});
            skLineSegment(sketch, "E67.right", {"start": v(-5143.89, 1127.99) * mm, "end": v(-5143.89, 1064.49) * mm});
            skPoint(sketch, "E68", {"position": v(-5143.89, 1096.24) * mm});
            skPoint(sketch, "E69", {"position": v(-5153.41, 1181.96) * mm});
            skPoint(sketch, "E70.0.1.0", {"position": v(-5153.41, 1308.96) * mm});
            skPoint(sketch, "E70.0.2.0", {"position": v(-5153.41, 1435.96) * mm});
            skLineSegment(sketch, "E70.direction1", {"start": v(-5153.41, 1181.96) * mm, "end": v(-5143.89, 1181.96) * mm, "construction": true});
            skLineSegment(sketch, "E70.direction2", {"start": v(-5153.41, 1181.96) * mm, "end": v(-5153.41, 1308.96) * mm, "construction": true});
            skPoint(sketch, "E71", {"position": v(-5153.41, 756.51) * mm});
            skPoint(sketch, "E72.0.1.0", {"position": v(-5153.41, 883.51) * mm});
            skPoint(sketch, "E72.0.2.0", {"position": v(-5153.41, 1010.51) * mm});
            skLineSegment(sketch, "E72.direction1", {"start": v(-5153.41, 756.51) * mm, "end": v(-5148.87, 756.51) * mm, "construction": true});
            skLineSegment(sketch, "E72.direction2", {"start": v(-5153.41, 756.51) * mm, "end": v(-5153.41, 883.51) * mm, "construction": true});
            skPoint(sketch, "E73", {"position": v(-5153.41, 1064.49) * mm});
            skPoint(sketch, "E74", {"position": v(-5153.41, 1499.46) * mm});
            skPoint(sketch, "E75.0.1.0", {"position": v(-5153.41, 1543.91) * mm});
            skLineSegment(sketch, "E75.direction1", {"start": v(-5153.41, 1499.46) * mm, "end": v(-5153.41, 1499.46) * mm});
            skLineSegment(sketch, "E75.direction2", {"start": v(-5153.41, 1499.46) * mm, "end": v(-5153.41, 1543.91) * mm, "construction": true});
            skPoint(sketch, "E76", {"position": v(-5153.41, 648.56) * mm});
            skPoint(sketch, "E77.0.1.0", {"position": v(-5153.41, 693.01) * mm});
            skLineSegment(sketch, "E77.direction1", {"start": v(-5153.41, 648.56) * mm, "end": v(-5153.41, 648.56) * mm});
            skLineSegment(sketch, "E77.direction2", {"start": v(-5153.41, 648.56) * mm, "end": v(-5153.41, 693.01) * mm, "construction": true});
            skPoint(sketch, "E78", {"position": v(-5153.41, 1074.01) * mm});
            skPoint(sketch, "E79.0.1.0", {"position": v(-5153.41, 1118.46) * mm});
            skLineSegment(sketch, "E79.direction1", {"start": v(-5153.41, 1074.01) * mm, "end": v(-5153.41, 1074.01) * mm});
            skLineSegment(sketch, "E79.direction2", {"start": v(-5153.41, 1074.01) * mm, "end": v(-5153.41, 1118.46) * mm, "construction": true});
            skLineSegment(sketch, "E80", {"start": v(-5153.41, 1489.94) * mm, "end": v(-5153.41, 1127.99) * mm});
            skLineSegment(sketch, "E81", {"start": v(-5153.41, 702.54) * mm, "end": v(-5153.41, 1064.49) * mm});
            skSolve(sketch);
        }
        {
            var Q0;
            Q0=sQuery(id+"F49.wireOp",VERTEX,"E61");
            var Q1;
            Q1=sQuery(id+"F49.wireOp",VERTEX,"E62.1.0.0");
            var Q2;
            Q2=sQuery(id+"F49.wireOp",VERTEX,"E62.2.0.0");
            var Q3;
            Q3=sQuery(id+"F49.wireOp",VERTEX,"E62.3.0.0");
            var Q4;
            Q4=sQuery(id+"F49.wireOp",VERTEX,"E62.4.0.0");
            var Q5;
            Q5=sQuery(id+"F49.wireOp",VERTEX,"E64.1.0.0");
            var Q6;
            Q6=sQuery(id+"F49.wireOp",VERTEX,"E64.1.1.0");
            var Q7;
            Q7=sQuery(id+"F49.wireOp",VERTEX,"E64.1.2.0");
            var Q8;
            Q8=sQuery(id+"F49.wireOp",VERTEX,"E64.1.3.0");
            var Q9;
            Q9=sQuery(id+"F49.wireOp",VERTEX,"E58.4.0.0");
            var Q10;
            Q10=sQuery(id+"F49.wireOp",VERTEX,"E58.3.0.0");
            var Q11;
            Q11=sQuery(id+"F49.wireOp",VERTEX,"E58.2.0.0");
            var Q12;
            Q12=sQuery(id+"F49.wireOp",VERTEX,"E58.1.0.0");
            var Q13;
            Q13=sQuery(id+"F49.wireOp",VERTEX,"E57");
            var Q14;
            Q14=sQuery(id+"F49.wireOp",VERTEX,"E64.0.3.0");
            var Q15;
            Q15=sQuery(id+"F49.wireOp",VERTEX,"E64.0.2.0");
            var Q16;
            Q16=sQuery(id+"F49.wireOp",VERTEX,"E64.0.1.0");
            var Q17;
            Q17=sQuery(id+"F49.wireOp",VERTEX,"E63");
            var Q18;
            Q18=sQuery(id+"F49.wireOp",VERTEX,"E64.1.4.0");
            var Q19;
            Q19=sQuery(id+"F49.wireOp",VERTEX,"E64.1.5.0");
            var Q20;
            Q20=sQuery(id+"F49.wireOp",VERTEX,"E64.1.6.0");
            var Q21;
            Q21=sQuery(id+"F49.wireOp",VERTEX,"E60.4.0.0");
            var Q22;
            Q22=sQuery(id+"F49.wireOp",VERTEX,"E60.3.0.0");
            var Q23;
            Q23=sQuery(id+"F49.wireOp",VERTEX,"E60.1.0.0");
            var Q24;
            Q24=sQuery(id+"F49.wireOp",VERTEX,"E59");
            var Q25;
            Q25=sQuery(id+"F49.wireOp",VERTEX,"E64.0.6.0");
            var Q26;
            Q26=sQuery(id+"F49.wireOp",VERTEX,"E64.0.5.0");
            var Q27;
            Q27=sQuery(id+"F49.wireOp",VERTEX,"E64.0.4.0");
            var Q28;
            Q28=sQuery(id+"F49.wireOp",VERTEX,"E60.2.0.0");
            var Q29;
            Q29=makeQuery(id+"F22.opExtrude","SWEPT_BODY",BODY,{"disambiguationData":[OSD([sQuery(id+"F21.wireOp",EDGE,"E17.bottom"),sQuery(id+"F21.wireOp",EDGE,"E17.top"),sQuery(id+"F21.wireOp",EDGE,"E17.left"),sQuery(id+"F21.wireOp",EDGE,"E17.right")])]});
            hole(context, id + "F50", {"style" : HoleStyle.C_SINK, "endStyle" : HoleEndStyle.THROUGH, "holeDiameter" : 3.97 * mm, "cSinkDiameter" : 8.73 * mm, "cSinkAngle" : 90 * degree, "locations" : qUnion([Q0, Q1, Q2, Q3, Q4, Q5, Q6, Q7, Q8, Q9, Q10, Q11, Q12, Q13, Q14, Q15, Q16, Q17, Q18, Q19, Q20, Q21, Q22, Q23, Q24, Q25, Q26, Q27, Q28]), "scope" : qUnion([Q29]), "isTappedThrough" : true, "startStyle" : HoleStartStyle.PART});
        }
        {
            var Q0;
            Q0=sQuery(id+"F49.wireOp",VERTEX,"E76");
            var Q1;
            Q1=sQuery(id+"F49.wireOp",VERTEX,"E77.0.1.0");
            var Q2;
            Q2=sQuery(id+"F49.wireOp",VERTEX,"E71");
            var Q3;
            Q3=sQuery(id+"F49.wireOp",VERTEX,"E72.0.1.0");
            var Q4;
            Q4=sQuery(id+"F49.wireOp",VERTEX,"E72.0.2.0");
            var Q5;
            Q5=sQuery(id+"F49.wireOp",VERTEX,"E78");
            var Q6;
            Q6=sQuery(id+"F49.wireOp",VERTEX,"E79.0.1.0");
            var Q7;
            Q7=sQuery(id+"F49.wireOp",VERTEX,"E69");
            var Q8;
            Q8=sQuery(id+"F49.wireOp",VERTEX,"E70.0.1.0");
            var Q9;
            Q9=sQuery(id+"F49.wireOp",VERTEX,"E70.0.2.0");
            var Q10;
            Q10=sQuery(id+"F49.wireOp",VERTEX,"E74");
            var Q11;
            Q11=sQuery(id+"F49.wireOp",VERTEX,"E75.0.1.0");
            var Q12;
            Q12=makeQuery(id+"F22.opExtrude","SWEPT_BODY",BODY,{"disambiguationData":[OSD([sQuery(id+"F21.wireOp",EDGE,"E17.bottom"),sQuery(id+"F21.wireOp",EDGE,"E17.top"),sQuery(id+"F21.wireOp",EDGE,"E17.left"),sQuery(id+"F21.wireOp",EDGE,"E17.right")])]});
            hole(context, id + "F51", {"style" : HoleStyle.C_SINK, "endStyle" : HoleEndStyle.THROUGH, "holeDiameter" : 3.97 * mm, "cSinkDiameter" : 8.73 * mm, "cSinkAngle" : 90 * degree, "locations" : qUnion([Q0, Q1, Q2, Q3, Q4, Q5, Q6, Q7, Q8, Q9, Q10, Q11]), "scope" : qUnion([Q12]), "isTappedThrough" : true, "startStyle" : HoleStartStyle.PART});
        }
        {
            var Q0;
            Q0=sQuery(id+"F46.wireOp",VERTEX,"E52");
            var Q1;
            Q1=sQuery(id+"F46.wireOp",VERTEX,"E53.1.0.0");
            var Q2;
            Q2=sQuery(id+"F46.wireOp",VERTEX,"E53.2.0.0");
            var Q3;
            Q3=sQuery(id+"F46.wireOp",VERTEX,"E39");
            var Q4;
            Q4=sQuery(id+"F46.wireOp",VERTEX,"E53.5.0.0");
            var Q5;
            Q5=sQuery(id+"F46.wireOp",VERTEX,"E53.6.0.0");
            var Q6;
            Q6=sQuery(id+"F46.wireOp",VERTEX,"E53.4.0.0");
            var Q7;
            Q7=sQuery(id+"F46.wireOp",VERTEX,"E51.1.0.0");
            var Q8;
            Q8=sQuery(id+"F46.wireOp",VERTEX,"E49");
            var Q9;
            Q9=sQuery(id+"F46.wireOp",VERTEX,"E50.1.0.0");
            var Q10;
            Q10=sQuery(id+"F46.wireOp",VERTEX,"E48");
            var Q11;
            Q11=sQuery(id+"F46.wireOp",VERTEX,"E44.2.0.0");
            var Q12;
            Q12=sQuery(id+"F46.wireOp",VERTEX,"E40");
            var Q13;
            Q13=sQuery(id+"F46.wireOp",VERTEX,"E42");
            var Q14;
            Q14=sQuery(id+"F46.wireOp",VERTEX,"E47.1.0.0");
            var Q15;
            Q15=sQuery(id+"F46.wireOp",VERTEX,"E46");
            var Q16;
            Q16=sQuery(id+"F46.wireOp",VERTEX,"E43");
            var Q17;
            Q17=sQuery(id+"F46.wireOp",VERTEX,"E41");
            var Q18;
            Q18=sQuery(id+"F46.wireOp",VERTEX,"E45.2.0.0");
            var Q19;
            Q19=makeQuery(id+"F3.opExtrude","SWEPT_BODY",BODY,{"disambiguationData":[OSD([sQuery(id+"F2.wireOp",EDGE,"E7.bottom"),sQuery(id+"F2.wireOp",EDGE,"E7.top"),sQuery(id+"F2.wireOp",EDGE,"E7.left"),sQuery(id+"F2.wireOp",EDGE,"E7.right")])]});
            hole(context, id + "F52", {"style" : HoleStyle.C_SINK, "endStyle" : HoleEndStyle.THROUGH, "holeDiameter" : 3.97 * mm, "cSinkDiameter" : 8.73 * mm, "cSinkAngle" : 90 * degree, "locations" : qUnion([Q0, Q1, Q2, Q3, Q4, Q5, Q6, Q7, Q8, Q9, Q10, Q11, Q12, Q13, Q14, Q15, Q16, Q17, Q18]), "scope" : qUnion([Q19]), "isTappedThrough" : true, "startStyle" : HoleStartStyle.PART});
        }
        {
            var Q0;
            Q0=makeQuery(id+"F46.imprint","IMPRINT",FACE,{"disambiguationData":[TD([[makeQuery(id+"F46.imprint","IMPRINT",EDGE,{"derivedFrom":makeQuery(id+"F3.opExtrude","CAP_EDGE",EDGE,{"disambiguationData":[OSD([sQuery(id+"F2.wireOp",EDGE,"E7.bottom")])],"isStart":true})}),1.0]])]});
            var sketch = newSketch(context, id + "F53", { "sketchPlane" : qUnion([Q0])});
            skPoint(sketch, "E82", {"position": v(-1297.28, 489.15) * mm});
            skPoint(sketch, "E83", {"position": v(-382.88, -120.45) * mm});
            skPoint(sketch, "E84", {"position": v(-1297.28, -120.45) * mm});
            skPoint(sketch, "E85", {"position": v(-382.88, 489.15) * mm});
            skLineSegment(sketch, "E86", {"start": v(-1297.28, 489.15) * mm, "end": v(-382.88, 489.15) * mm});
            skLineSegment(sketch, "E87", {"start": v(-1297.28, -120.45) * mm, "end": v(-382.88, -120.45) * mm});
            skLineSegment(sketch, "E88", {"start": v(-382.88, 489.15) * mm, "end": v(-382.88, -120.45) * mm});
            skLineSegment(sketch, "E89", {"start": v(-1297.28, 489.15) * mm, "end": v(-1297.28, -120.45) * mm});
            skLineSegment(sketch, "E90", {"start": v(-1297.28, 184.35) * mm, "end": v(-382.88, 184.35) * mm});
            skLineSegment(sketch, "E91", {"start": v(-840.08, 489.15) * mm, "end": v(-840.08, -120.45) * mm});
            skLineSegment(sketch, "E92.bottom", {"start": v(-1166.38, -73.9) * mm, "end": v(-1250.38, -73.9) * mm});
            skLineSegment(sketch, "E92.top", {"start": v(-1166.38, -1.9) * mm, "end": v(-1250.38, -1.9) * mm});
            skLineSegment(sketch, "E92.left", {"start": v(-1166.38, -73.9) * mm, "end": v(-1166.38, -1.9) * mm});
            skLineSegment(sketch, "E92.right", {"start": v(-1250.38, -73.9) * mm, "end": v(-1250.38, -1.9) * mm});
            skPoint(sketch, "E92.middle", {"position": v(-1208.38, -37.9) * mm});
            skCircle(sketch, "E93", {"center": v(-1250.38, -1.9) * mm, "radius": 4.76 * mm});
            skCircle(sketch, "E94", {"center": v(-1166.38, -1.9) * mm, "radius": 4.76 * mm});
            skCircle(sketch, "E95", {"center": v(-1250.38, -73.9) * mm, "radius": 4.76 * mm});
            skCircle(sketch, "E96", {"center": v(-1166.38, -73.9) * mm, "radius": 4.76 * mm});
            skCircle(sketch, "E97.MirrorC", {"center": v(-513.78, -1.9) * mm, "radius": 4.76 * mm});
            skCircle(sketch, "E98.MirrorC", {"center": v(-429.78, -1.9) * mm, "radius": 4.76 * mm});
            skCircle(sketch, "E99.MirrorC", {"center": v(-429.78, -73.9) * mm, "radius": 4.76 * mm});
            skCircle(sketch, "E100.MirrorC", {"center": v(-513.78, -73.9) * mm, "radius": 4.76 * mm});
            skPoint(sketch, "E101.MirrorP", {"position": v(-471.78, -37.9) * mm});
            skLineSegment(sketch, "E102.MirrorCS", {"start": v(-513.78, -1.9) * mm, "end": v(-429.78, -1.9) * mm});
            skLineSegment(sketch, "E103.MirrorCS", {"start": v(-429.78, -73.9) * mm, "end": v(-429.78, -1.9) * mm});
            skLineSegment(sketch, "E104.MirrorCS", {"start": v(-513.78, -73.9) * mm, "end": v(-513.78, -1.9) * mm});
            skLineSegment(sketch, "E105.MirrorCS", {"start": v(-513.78, -73.9) * mm, "end": v(-429.78, -73.9) * mm});
            skCircle(sketch, "E106.MirrorC", {"center": v(-513.78, 442.6) * mm, "radius": 4.76 * mm});
            skCircle(sketch, "E107.MirrorC", {"center": v(-513.78, 370.6) * mm, "radius": 4.76 * mm});
            skCircle(sketch, "E108.MirrorC", {"center": v(-429.78, 370.6) * mm, "radius": 4.76 * mm});
            skCircle(sketch, "E109.MirrorC", {"center": v(-1250.38, 370.6) * mm, "radius": 4.76 * mm});
            skCircle(sketch, "E110.MirrorC", {"center": v(-1166.38, 370.6) * mm, "radius": 4.76 * mm});
            skCircle(sketch, "E111.MirrorC", {"center": v(-1166.38, 442.6) * mm, "radius": 4.76 * mm});
            skCircle(sketch, "E112.MirrorC", {"center": v(-429.78, 442.6) * mm, "radius": 4.76 * mm});
            skCircle(sketch, "E113.MirrorC", {"center": v(-1250.38, 442.6) * mm, "radius": 4.76 * mm});
            skLineSegment(sketch, "E114.MirrorCS", {"start": v(-513.78, 442.6) * mm, "end": v(-513.78, 370.6) * mm});
            skLineSegment(sketch, "E115.MirrorCS", {"start": v(-429.78, 442.6) * mm, "end": v(-429.78, 370.6) * mm});
            skLineSegment(sketch, "E116.MirrorCS", {"start": v(-1166.38, 442.6) * mm, "end": v(-1166.38, 370.6) * mm});
            skLineSegment(sketch, "E117.MirrorCS", {"start": v(-513.78, 370.6) * mm, "end": v(-429.78, 370.6) * mm});
            skLineSegment(sketch, "E118.MirrorCS", {"start": v(-1250.38, 442.6) * mm, "end": v(-1250.38, 370.6) * mm});
            skLineSegment(sketch, "E119.MirrorCS", {"start": v(-1166.38, 370.6) * mm, "end": v(-1250.38, 370.6) * mm});
            skPoint(sketch, "E120.MirrorP", {"position": v(-471.78, 406.6) * mm});
            skLineSegment(sketch, "E121.MirrorCS", {"start": v(-1166.38, 442.6) * mm, "end": v(-1250.38, 442.6) * mm});
            skPoint(sketch, "E122.MirrorP", {"position": v(-1208.38, 406.6) * mm});
            skLineSegment(sketch, "E123.MirrorCS", {"start": v(-513.78, 442.6) * mm, "end": v(-429.78, 442.6) * mm});
            skSolve(sketch);
        }
        {
            var Q0;
            Q0=sQuery(id+"F53.wireOp",VERTEX,"E92.bottom.end");
            var Q1;
            Q1=sQuery(id+"F53.wireOp",VERTEX,"E96.center");
            var Q2;
            Q2=sQuery(id+"F53.wireOp",VERTEX,"E94.center");
            var Q3;
            Q3=sQuery(id+"F53.wireOp",VERTEX,"E92.right.end");
            var Q4;
            Q4=makeQuery(id+"F3.opExtrude","SWEPT_BODY",BODY,{"disambiguationData":[OSD([sQuery(id+"F2.wireOp",EDGE,"E7.bottom"),sQuery(id+"F2.wireOp",EDGE,"E7.top"),sQuery(id+"F2.wireOp",EDGE,"E7.left"),sQuery(id+"F2.wireOp",EDGE,"E7.right")])]});
            hole(context, id + "F54", {"style" : HoleStyle.SIMPLE, "endStyle" : HoleEndStyle.THROUGH, "holeDiameter" : 12.7 * mm, "locations" : qUnion([Q0, Q1, Q2, Q3]), "scope" : qUnion([Q4]), "isTappedThrough" : true, "startStyle" : HoleStartStyle.PART});
        }
        {
            var Q0;
            Q0=sQuery(id+"F53.wireOp",VERTEX,"E109.MirrorC.center");
            var Q1;
            Q1=sQuery(id+"F53.wireOp",VERTEX,"E110.MirrorC.center");
            var Q2;
            Q2=sQuery(id+"F53.wireOp",VERTEX,"E111.MirrorC.center");
            var Q3;
            Q3=sQuery(id+"F53.wireOp",VERTEX,"E118.MirrorCS.start");
            var Q4;
            Q4=sQuery(id+"F53.wireOp",VERTEX,"E100.MirrorC.center");
            var Q5;
            Q5=sQuery(id+"F53.wireOp",VERTEX,"E97.MirrorC.center");
            var Q6;
            Q6=sQuery(id+"F53.wireOp",VERTEX,"E98.MirrorC.center");
            var Q7;
            Q7=sQuery(id+"F53.wireOp",VERTEX,"E103.MirrorCS.start");
            var Q8;
            Q8=sQuery(id+"F53.wireOp",VERTEX,"E115.MirrorCS.end");
            var Q9;
            Q9=sQuery(id+"F53.wireOp",VERTEX,"E123.MirrorCS.end");
            var Q10;
            Q10=sQuery(id+"F53.wireOp",VERTEX,"E114.MirrorCS.start");
            var Q11;
            Q11=sQuery(id+"F53.wireOp",VERTEX,"E107.MirrorC.center");
            var Q12;
            Q12=makeQuery(id+"F3.opExtrude","SWEPT_BODY",BODY,{"disambiguationData":[OSD([sQuery(id+"F2.wireOp",EDGE,"E7.bottom"),sQuery(id+"F2.wireOp",EDGE,"E7.top"),sQuery(id+"F2.wireOp",EDGE,"E7.left"),sQuery(id+"F2.wireOp",EDGE,"E7.right")])]});
            hole(context, id + "F55", {"style" : HoleStyle.SIMPLE, "endStyle" : HoleEndStyle.THROUGH, "holeDiameter" : 12.7 * mm, "locations" : qUnion([Q0, Q1, Q2, Q3, Q4, Q5, Q6, Q7, Q8, Q9, Q10, Q11]), "scope" : qUnion([Q12]), "isTappedThrough" : true, "startStyle" : HoleStartStyle.PART});
        }
        {
            var Q0;
            Q0=qCreatedBy(makeId("Front.planeOp"),FACE);
            var sketch = newSketch(context, id + "F56", { "sketchPlane" : qUnion([Q0])});
            skLineSegment(sketch, "E124.bottom", {"start": v(-3510.87, 1085.09) * mm, "end": v(-1072.47, 1085.09) * mm});
            skLineSegment(sketch, "E124.top", {"start": v(-3510.87, -134.11) * mm, "end": v(-1072.47, -134.11) * mm});
            skLineSegment(sketch, "E124.left", {"start": v(-3510.87, 1085.09) * mm, "end": v(-3510.87, -134.11) * mm});
            skLineSegment(sketch, "E124.right", {"start": v(-1072.47, 1085.09) * mm, "end": v(-1072.47, -134.11) * mm});
            skSolve(sketch);
        }
        {
            var Q0;
            Q0 = qSketchRegion(id + "F56", true);
            extrude(context, id + "F57", {"entities" : qUnion([Q0]), "depth" : 3.17 * mm});
        }
    });
